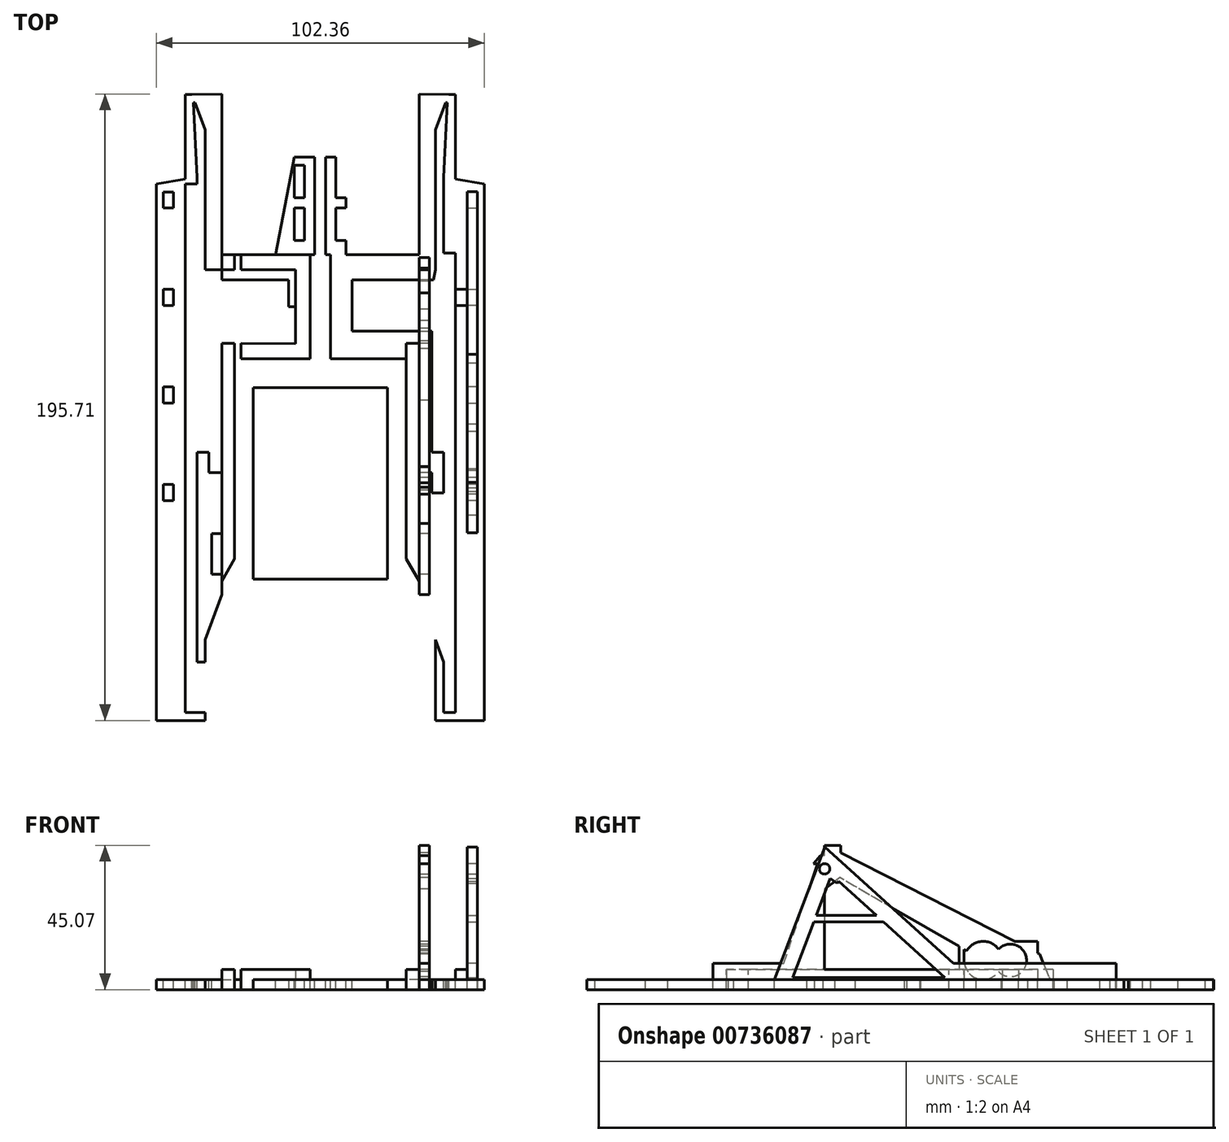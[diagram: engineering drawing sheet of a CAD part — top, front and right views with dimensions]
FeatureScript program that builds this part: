
annotation { "Feature Type Name" : "Feature", "Feature Type Description" : "" }
export const myFeature = defineFeature(function(context is Context, id is Id, definition is map)
    precondition{}
    {
        {
            var Q0;
            Q0=qCreatedBy(makeId("Top.planeOp"),FACE);
            var sketch = newSketch(context, id + "F0", { "sketchPlane" : qUnion([Q0])});
            skLineSegment(sketch, "E0", {"start": v(0, 0) * mm, "end": v(0, -23) * mm});
            skLineSegment(sketch, "E1", {"start": v(0, -23) * mm, "end": v(-4, -23) * mm});
            skLineSegment(sketch, "E2", {"start": v(-4, -23) * mm, "end": v(-4, -27.75) * mm});
            skLineSegment(sketch, "E3", {"start": v(-4, -27.75) * mm, "end": v(-6, -27.75) * mm});
            skLineSegment(sketch, "E4", {"start": v(-6, -27.75) * mm, "end": v(-6, -23) * mm});
            skLineSegment(sketch, "E5", {"start": v(0, -11.5) * mm, "end": v(-23.04, -11.5) * mm});
            skLineSegment(sketch, "E6", {"start": v(-23.04, -11.5) * mm, "end": v(-23.04, -23.02) * mm});
            skLineSegment(sketch, "E7", {"start": v(-23.04, -23.02) * mm, "end": v(-6, -23) * mm});
            skLineSegment(sketch, "E8.MirrorCS", {"start": v(0, 0) * mm, "end": v(-4, 0) * mm});
            skLineSegment(sketch, "E9.MirrorCS", {"start": v(-4, 0) * mm, "end": v(-4, 4.75) * mm});
            skLineSegment(sketch, "E10.MirrorCS", {"start": v(-6, 4.75) * mm, "end": v(-6, 0) * mm});
            skLineSegment(sketch, "E11.MirrorCS", {"start": v(-4, 4.75) * mm, "end": v(-6, 4.75) * mm});
            skLineSegment(sketch, "E12.MirrorCS", {"start": v(-23.04, -11.5) * mm, "end": v(-23.04, 0.02) * mm});
            skLineSegment(sketch, "E13.MirrorCS", {"start": v(-23.04, 0.02) * mm, "end": v(-6, 0) * mm});
            skLineSegment(sketch, "E14", {"start": v(0, -6.14) * mm, "end": v(4, -6.14) * mm});
            skLineSegment(sketch, "E15", {"start": v(0, 0) * mm, "end": v(5.14, 0) * mm});
            skLineSegment(sketch, "E16", {"start": v(5.14, 0) * mm, "end": v(4, -6.14) * mm});
            skLineSegment(sketch, "E17", {"start": v(4, -6.14) * mm, "end": v(7.68, -6.14) * mm});
            skLineSegment(sketch, "E18", {"start": v(7.68, -6.14) * mm, "end": v(7.68, -53.77) * mm});
            skLineSegment(sketch, "E19", {"start": v(7.68, -53.77) * mm, "end": v(7.68, -63.3) * mm});
            skLineSegment(sketch, "E20", {"start": v(7.68, -63.3) * mm, "end": v(0, -63.3) * mm});
            skLineSegment(sketch, "E21", {"start": v(0, -63.3) * mm, "end": v(0, -23) * mm});
            skLineSegment(sketch, "E22", {"start": v(-4, -27.75) * mm, "end": v(-4, -63.3) * mm});
            skLineSegment(sketch, "E23", {"start": v(-4, -63.3) * mm, "end": v(0, -63.3) * mm});
            skLineSegment(sketch, "E24", {"start": v(0, -23) * mm, "end": v(3.18, -23) * mm});
            skLineSegment(sketch, "E25", {"start": v(3.18, -23) * mm, "end": v(3.18, -40.78) * mm});
            skLineSegment(sketch, "E26", {"start": v(3.18, -40.78) * mm, "end": v(0, -40.78) * mm});
            skLineSegment(sketch, "E27", {"start": v(0, -63.3) * mm, "end": v(0, -101.4) * mm});
            skLineSegment(sketch, "E28", {"start": v(0, -101.4) * mm, "end": v(7.68, -122.5) * mm});
            skLineSegment(sketch, "E29", {"start": v(7.68, -122.5) * mm, "end": v(7.68, -63.3) * mm});
            skLineSegment(sketch, "E30", {"start": v(-4, -63.3) * mm, "end": v(-4, -90.28) * mm});
            skLineSegment(sketch, "E31", {"start": v(-4, -90.28) * mm, "end": v(0, -97.2) * mm});
            skLineSegment(sketch, "E32", {"start": v(0, -63.3) * mm, "end": v(3.18, -63.3) * mm});
            skPoint(sketch, "E32.endSnap0", {"position": v(3.18, -31.9) * mm});
            skLineSegment(sketch, "E33", {"start": v(0, -82.34) * mm, "end": v(3.18, -82.34) * mm});
            skLineSegment(sketch, "E34", {"start": v(3.18, -82.34) * mm, "end": v(3.18, -95.04) * mm});
            skLineSegment(sketch, "E35", {"start": v(3.18, -95.04) * mm, "end": v(0, -95.04) * mm});
            skLineSegment(sketch, "E36", {"start": v(7.68, -63.3) * mm, "end": v(11.11, -63.3) * mm});
            skLineSegment(sketch, "E37", {"start": v(7.68, -6.14) * mm, "end": v(7.68, -56.94) * mm});
            skLineSegment(sketch, "E38", {"start": v(7.68, -56.94) * mm, "end": v(4, -56.94) * mm});
            skLineSegment(sketch, "E39", {"start": v(4, -56.94) * mm, "end": v(4, -6.14) * mm});
            skLineSegment(sketch, "E40", {"start": v(4, -56.94) * mm, "end": v(4, -69.64) * mm});
            skLineSegment(sketch, "E41", {"start": v(4, -69.64) * mm, "end": v(7.68, -69.64) * mm});
            skLineSegment(sketch, "E42", {"start": v(0, -23) * mm, "end": v(0, -27.75) * mm});
            skLineSegment(sketch, "E43", {"start": v(-4, -27.75) * mm, "end": v(0, -27.75) * mm});
            skLineSegment(sketch, "E44", {"start": v(-6, -27.75) * mm, "end": v(-27.59, -27.75) * mm});
            skLineSegment(sketch, "E45.MirrorCS", {"start": v(-4, 4.75) * mm, "end": v(0, 4.75) * mm});
            skLineSegment(sketch, "E46.MirrorCS", {"start": v(-6, 4.75) * mm, "end": v(-27.59, 4.75) * mm});
            skLineSegment(sketch, "E47", {"start": v(0, 4.75) * mm, "end": v(0, 0) * mm});
            skLineSegment(sketch, "E48", {"start": v(-27.59, 4.75) * mm, "end": v(-27.59, -27.75) * mm});
            skLineSegment(sketch, "E49", {"start": v(7.68, -56.94) * mm, "end": v(7.68, -138.22) * mm});
            skLineSegment(sketch, "E50", {"start": v(7.68, -138.22) * mm, "end": v(11.37, -138.22) * mm});
            skLineSegment(sketch, "E51", {"start": v(11.37, -138.22) * mm, "end": v(11.37, 24.34) * mm});
            skLineSegment(sketch, "E52", {"start": v(11.37, 24.34) * mm, "end": v(7.68, 24.34) * mm});
            skLineSegment(sketch, "E53", {"start": v(7.68, 24.34) * mm, "end": v(7.68, -6.14) * mm});
            skLineSegment(sketch, "E54", {"start": v(7.68, -122.5) * mm, "end": v(5.14, -122.5) * mm});
            skLineSegment(sketch, "E55", {"start": v(5.14, -122.5) * mm, "end": v(5.14, -115.52) * mm});
            skLineSegment(sketch, "E56", {"start": v(7.68, -138.22) * mm, "end": v(7.68, -140.76) * mm});
            skLineSegment(sketch, "E57", {"start": v(7.68, -138.22) * mm, "end": v(5.14, -138.22) * mm});
            skLineSegment(sketch, "E58", {"start": v(5.14, -122.5) * mm, "end": v(5.14, -140.76) * mm});
            skLineSegment(sketch, "E59", {"start": v(5.14, -140.76) * mm, "end": v(20.38, -140.76) * mm});
            skLineSegment(sketch, "E60", {"start": v(20.38, -140.76) * mm, "end": v(20.38, 24.34) * mm});
            skLineSegment(sketch, "E61", {"start": v(20.38, 24.34) * mm, "end": v(20.38, 26.88) * mm});
            skLineSegment(sketch, "E62", {"start": v(20.38, 26.88) * mm, "end": v(5.14, 26.88) * mm});
            skLineSegment(sketch, "E63", {"start": v(5.14, 26.88) * mm, "end": v(5.14, 0) * mm});
            skLineSegment(sketch, "E64", {"start": v(0, 4.75) * mm, "end": v(0, 30.15) * mm});
            skLineSegment(sketch, "E65", {"start": v(0, 30.15) * mm, "end": v(20.38, 26.88) * mm});
            skLineSegment(sketch, "E66", {"start": v(7.68, 24.34) * mm, "end": v(5.14, 26.88) * mm});
            skLineSegment(sketch, "E67", {"start": v(7.68, 24.34) * mm, "end": v(7.68, 28.92) * mm});
            skLineSegment(sketch, "E68", {"start": v(5.14, 26.88) * mm, "end": v(5.14, 52.28) * mm});
            skLineSegment(sketch, "E69", {"start": v(5.14, 52.28) * mm, "end": v(8.83, 52.28) * mm});
            skLineSegment(sketch, "E70", {"start": v(8.83, 52.28) * mm, "end": v(7.68, 28.92) * mm});
            skLineSegment(sketch, "E71", {"start": v(11.37, 24.34) * mm, "end": v(11.37, 54.82) * mm});
            skLineSegment(sketch, "E72", {"start": v(11.37, 54.82) * mm, "end": v(9.3, 54.82) * mm});
            skLineSegment(sketch, "E73", {"start": v(9.3, 54.82) * mm, "end": v(9.3, 28.66) * mm});
            skLineSegment(sketch, "E74.bottom", {"start": v(-4, -27.75) * mm, "end": v(-57.6, -27.75) * mm});
            skLineSegment(sketch, "E74.top", {"start": v(-4, -96.58) * mm, "end": v(-57.6, -96.58) * mm});
            skLineSegment(sketch, "E74.left", {"start": v(-4, -27.75) * mm, "end": v(-4, -96.58) * mm});
            skLineSegment(sketch, "E74.right", {"start": v(-57.6, -27.75) * mm, "end": v(-57.6, -96.58) * mm});
            skLineSegment(sketch, "E75", {"start": v(-30.8, -96.58) * mm, "end": v(-30.8, -27.75) * mm});
            skLineSegment(sketch, "E76.MirrorCS", {"start": v(-69.28, -6.14) * mm, "end": v(-69.28, -56.94) * mm});
            skLineSegment(sketch, "E77.MirrorCS", {"start": v(-69.28, -6.14) * mm, "end": v(-69.28, -53.77) * mm});
            skLineSegment(sketch, "E78.MirrorCS", {"start": v(-65.6, -56.94) * mm, "end": v(-65.6, -6.14) * mm});
            skLineSegment(sketch, "E79.MirrorCS", {"start": v(-65.6, -6.14) * mm, "end": v(-69.28, -6.14) * mm});
            skLineSegment(sketch, "E80.MirrorCS", {"start": v(-57.6, 4.75) * mm, "end": v(-61.6, 4.75) * mm});
            skLineSegment(sketch, "E81.MirrorCS", {"start": v(-61.6, 0) * mm, "end": v(-66.74, 0) * mm});
            skLineSegment(sketch, "E82.MirrorCS", {"start": v(-61.6, 4.75) * mm, "end": v(-61.6, 0) * mm});
            skLineSegment(sketch, "E83.MirrorCS", {"start": v(-57.6, 4.75) * mm, "end": v(-55.6, 4.75) * mm});
            skLineSegment(sketch, "E84.MirrorCS", {"start": v(-61.6, 0) * mm, "end": v(-57.6, 0) * mm});
            skLineSegment(sketch, "E85.MirrorCS", {"start": v(-57.6, 0) * mm, "end": v(-57.6, 4.75) * mm});
            skLineSegment(sketch, "E86.MirrorCS", {"start": v(-55.6, 4.75) * mm, "end": v(-55.6, 0) * mm});
            skLineSegment(sketch, "E87.MirrorCS", {"start": v(-61.6, -6.14) * mm, "end": v(-65.6, -6.14) * mm});
            skLineSegment(sketch, "E88.MirrorCS", {"start": v(-66.74, 0) * mm, "end": v(-65.6, -6.14) * mm});
            skLineSegment(sketch, "E89.MirrorCS", {"start": v(-61.6, 0) * mm, "end": v(-61.6, -23) * mm});
            skLineSegment(sketch, "E90.MirrorCS", {"start": v(-55.6, 4.75) * mm, "end": v(-34, 4.75) * mm});
            skLineSegment(sketch, "E91.MirrorCS", {"start": v(-61.6, 4.75) * mm, "end": v(-61.6, 30.15) * mm});
            skLineSegment(sketch, "E92.MirrorCS", {"start": v(-34, 4.75) * mm, "end": v(-34, -27.75) * mm});
            skLineSegment(sketch, "E93.MirrorCS", {"start": v(-66.74, 26.88) * mm, "end": v(-66.74, 0) * mm});
            skLineSegment(sketch, "E94.MirrorCS", {"start": v(-72.96, -138.22) * mm, "end": v(-72.96, 24.34) * mm});
            skLineSegment(sketch, "E95.MirrorCS", {"start": v(-81.98, -140.76) * mm, "end": v(-81.98, 24.34) * mm});
            skLineSegment(sketch, "E96.MirrorCS", {"start": v(-69.28, 24.34) * mm, "end": v(-69.28, -6.14) * mm});
            skLineSegment(sketch, "E97.MirrorCS", {"start": v(-38.56, 0.02) * mm, "end": v(-55.6, 0) * mm});
            skLineSegment(sketch, "E98.MirrorCS", {"start": v(-38.56, -11.5) * mm, "end": v(-38.56, 0.02) * mm});
            skLineSegment(sketch, "E99.MirrorCS", {"start": v(-69.28, 24.34) * mm, "end": v(-66.74, 26.88) * mm});
            skLineSegment(sketch, "E100.MirrorCS", {"start": v(-72.96, 24.34) * mm, "end": v(-69.28, 24.34) * mm});
            skLineSegment(sketch, "E101.MirrorCS", {"start": v(-81.98, 24.34) * mm, "end": v(-81.98, 26.88) * mm});
            skLineSegment(sketch, "E102.MirrorCS", {"start": v(-81.98, 26.88) * mm, "end": v(-66.74, 26.88) * mm});
            skLineSegment(sketch, "E103.MirrorCS", {"start": v(-69.28, 24.34) * mm, "end": v(-69.28, 28.92) * mm});
            skLineSegment(sketch, "E104.MirrorCS", {"start": v(-66.74, 52.28) * mm, "end": v(-70.42, 52.28) * mm});
            skLineSegment(sketch, "E105.MirrorCS", {"start": v(-61.6, 30.15) * mm, "end": v(-81.98, 26.88) * mm});
            skLineSegment(sketch, "E106.MirrorCS", {"start": v(-72.96, 24.34) * mm, "end": v(-72.96, 54.82) * mm});
            skLineSegment(sketch, "E107.MirrorCS", {"start": v(-70.42, 52.28) * mm, "end": v(-69.28, 28.92) * mm});
            skLineSegment(sketch, "E108.MirrorCS", {"start": v(-66.74, 26.88) * mm, "end": v(-66.74, 52.28) * mm});
            skLineSegment(sketch, "E109.MirrorCS", {"start": v(-70.9, 54.82) * mm, "end": v(-70.9, 28.66) * mm});
            skLineSegment(sketch, "E110.MirrorCS", {"start": v(-69.28, -138.22) * mm, "end": v(-69.28, -140.76) * mm});
            skLineSegment(sketch, "E111.MirrorCS", {"start": v(-69.28, -138.22) * mm, "end": v(-66.74, -138.22) * mm});
            skLineSegment(sketch, "E112.MirrorCS", {"start": v(-69.28, -122.5) * mm, "end": v(-66.74, -122.5) * mm});
            skLineSegment(sketch, "E113.MirrorCS", {"start": v(-66.74, -140.76) * mm, "end": v(-81.98, -140.76) * mm});
            skLineSegment(sketch, "E114.MirrorCS", {"start": v(-69.28, -138.22) * mm, "end": v(-72.96, -138.22) * mm});
            skLineSegment(sketch, "E115.MirrorCS", {"start": v(-61.6, -101.4) * mm, "end": v(-69.28, -122.5) * mm});
            skLineSegment(sketch, "E116.MirrorCS", {"start": v(-66.74, -122.5) * mm, "end": v(-66.74, -140.76) * mm});
            skLineSegment(sketch, "E117.MirrorCS", {"start": v(-66.74, -122.5) * mm, "end": v(-66.74, -115.52) * mm});
            skLineSegment(sketch, "E118.MirrorCS", {"start": v(-57.6, -63.3) * mm, "end": v(-61.6, -63.3) * mm});
            skLineSegment(sketch, "E119.MirrorCS", {"start": v(-69.28, -56.94) * mm, "end": v(-65.6, -56.94) * mm});
            skLineSegment(sketch, "E120.MirrorCS", {"start": v(-64.77, -23) * mm, "end": v(-64.77, -40.78) * mm});
            skLineSegment(sketch, "E121.MirrorCS", {"start": v(-65.6, -69.64) * mm, "end": v(-69.28, -69.64) * mm});
            skLineSegment(sketch, "E122.MirrorCS", {"start": v(-69.28, -122.5) * mm, "end": v(-69.28, -63.3) * mm});
            skLineSegment(sketch, "E123.MirrorCS", {"start": v(-64.77, -40.78) * mm, "end": v(-61.6, -40.78) * mm});
            skLineSegment(sketch, "E124.MirrorCS", {"start": v(-61.6, -63.3) * mm, "end": v(-64.77, -63.3) * mm});
            skLineSegment(sketch, "E125.MirrorCS", {"start": v(-69.28, -63.3) * mm, "end": v(-72.7, -63.3) * mm});
            skLineSegment(sketch, "E126.MirrorCS", {"start": v(-69.28, -63.3) * mm, "end": v(-61.6, -63.3) * mm});
            skLineSegment(sketch, "E127.MirrorCS", {"start": v(-69.28, -53.77) * mm, "end": v(-69.28, -63.3) * mm});
            skLineSegment(sketch, "E128.MirrorCS", {"start": v(-61.6, -63.3) * mm, "end": v(-61.6, -101.4) * mm});
            skLineSegment(sketch, "E129.MirrorCS", {"start": v(-69.28, -56.94) * mm, "end": v(-69.28, -138.22) * mm});
            skLineSegment(sketch, "E130.MirrorCS", {"start": v(-65.6, -56.94) * mm, "end": v(-65.6, -69.64) * mm});
            skLineSegment(sketch, "E131.MirrorCS", {"start": v(-61.6, -63.3) * mm, "end": v(-61.6, -23) * mm});
            skLineSegment(sketch, "E132.MirrorCS", {"start": v(-57.6, -90.28) * mm, "end": v(-61.6, -97.2) * mm});
            skLineSegment(sketch, "E133.MirrorCS", {"start": v(-61.6, -23) * mm, "end": v(-64.77, -23) * mm});
            skLineSegment(sketch, "E134.MirrorCS", {"start": v(-61.6, -23) * mm, "end": v(-57.6, -23) * mm});
            skLineSegment(sketch, "E135.MirrorCS", {"start": v(-38.56, -23.02) * mm, "end": v(-55.6, -23) * mm});
            skLineSegment(sketch, "E136.MirrorCS", {"start": v(-38.56, -11.5) * mm, "end": v(-38.56, -23.02) * mm});
            skLineSegment(sketch, "E137.MirrorCS", {"start": v(-55.6, -27.75) * mm, "end": v(-55.6, -23) * mm});
            skLineSegment(sketch, "E138.MirrorCS", {"start": v(-57.6, -23) * mm, "end": v(-57.6, -27.75) * mm});
            skLineSegment(sketch, "E139.MirrorCS", {"start": v(-61.6, -11.5) * mm, "end": v(-38.56, -11.5) * mm});
            skLineSegment(sketch, "E140.MirrorCS", {"start": v(-61.6, -23) * mm, "end": v(-61.6, -27.75) * mm});
            skLineSegment(sketch, "E141.MirrorCS", {"start": v(-66.74, 26.88) * mm, "end": v(-66.74, 52.17) * mm});
            skLineSegment(sketch, "E142.MirrorCS", {"start": v(-57.6, -27.75) * mm, "end": v(-61.6, -27.75) * mm});
            skLineSegment(sketch, "E143.MirrorCS", {"start": v(-61.6, -82.34) * mm, "end": v(-64.77, -82.34) * mm});
            skLineSegment(sketch, "E144.MirrorCS", {"start": v(-64.77, -95.04) * mm, "end": v(-61.6, -95.04) * mm});
            skLineSegment(sketch, "E145.MirrorCS", {"start": v(-64.77, -82.34) * mm, "end": v(-64.77, -95.04) * mm});
            skPoint(sketch, "E146.MirrorP", {"position": v(-64.77, -31.9) * mm});
            skLineSegment(sketch, "E147.MirrorCS", {"start": v(-72.96, 54.82) * mm, "end": v(-70.9, 54.82) * mm});
            skLineSegment(sketch, "E148.bottom", {"start": v(-30.8, -96.58) * mm, "end": v(-51.78, -96.58) * mm});
            skLineSegment(sketch, "E148.top", {"start": v(-30.8, -36.78) * mm, "end": v(-51.78, -36.78) * mm});
            skLineSegment(sketch, "E148.left", {"start": v(-30.8, -96.58) * mm, "end": v(-30.8, -36.78) * mm});
            skLineSegment(sketch, "E148.right", {"start": v(-51.78, -96.58) * mm, "end": v(-51.78, -36.78) * mm});
            skLineSegment(sketch, "E149.MirrorCS", {"start": v(-30.8, -36.78) * mm, "end": v(-9.82, -36.78) * mm});
            skLineSegment(sketch, "E150.MirrorCS", {"start": v(-9.82, -96.58) * mm, "end": v(-9.82, -36.78) * mm});
            skLineSegment(sketch, "E151", {"start": v(11.37, 24.34) * mm, "end": v(15.05, 24.34) * mm});
            skLineSegment(sketch, "E152", {"start": v(15.05, 24.34) * mm, "end": v(18.27, 24.34) * mm});
            skLineSegment(sketch, "E153", {"start": v(18.27, 24.34) * mm, "end": v(20.38, 24.34) * mm});
            skLineSegment(sketch, "E154", {"start": v(15.05, 24.34) * mm, "end": v(15.05, 19.36) * mm});
            skLineSegment(sketch, "E155", {"start": v(15.05, 19.36) * mm, "end": v(18.27, 19.36) * mm});
            skLineSegment(sketch, "E156", {"start": v(18.27, 19.36) * mm, "end": v(18.27, 24.34) * mm});
            skLineSegment(sketch, "E157", {"start": v(16.66, 19.36) * mm, "end": v(16.66, -6.04) * mm});
            skLineSegment(sketch, "E158", {"start": v(16.66, -6.04) * mm, "end": v(18.27, -6.04) * mm});
            skLineSegment(sketch, "E159", {"start": v(18.27, -6.04) * mm, "end": v(18.27, -11.12) * mm});
            skLineSegment(sketch, "E160", {"start": v(18.27, -11.12) * mm, "end": v(15.05, -11.12) * mm});
            skLineSegment(sketch, "E161", {"start": v(15.05, -11.12) * mm, "end": v(15.05, -6.04) * mm});
            skLineSegment(sketch, "E162", {"start": v(15.05, -6.04) * mm, "end": v(16.66, -6.04) * mm});
            skLineSegment(sketch, "E163", {"start": v(16.66, -11.12) * mm, "end": v(16.66, -36.52) * mm});
            skLineSegment(sketch, "E164", {"start": v(16.66, -36.52) * mm, "end": v(18.27, -36.52) * mm});
            skLineSegment(sketch, "E165", {"start": v(18.27, -36.52) * mm, "end": v(15.05, -36.52) * mm});
            skLineSegment(sketch, "E166", {"start": v(15.05, -36.52) * mm, "end": v(15.05, -41.6) * mm});
            skLineSegment(sketch, "E167", {"start": v(15.05, -41.6) * mm, "end": v(18.27, -41.6) * mm});
            skLineSegment(sketch, "E168", {"start": v(18.27, -41.6) * mm, "end": v(18.27, -36.52) * mm});
            skLineSegment(sketch, "E169", {"start": v(15.05, -39.06) * mm, "end": v(18.27, -39.06) * mm});
            skLineSegment(sketch, "E170.MirrorCS", {"start": v(16.66, -67) * mm, "end": v(16.66, -41.6) * mm});
            skLineSegment(sketch, "E171.MirrorCS", {"start": v(18.27, -41.6) * mm, "end": v(15.05, -41.6) * mm});
            skLineSegment(sketch, "E172.MirrorCS", {"start": v(15.05, -41.6) * mm, "end": v(15.05, -36.52) * mm});
            skLineSegment(sketch, "E173", {"start": v(16.66, -67) * mm, "end": v(18.27, -67) * mm});
            skLineSegment(sketch, "E174", {"start": v(16.66, -67) * mm, "end": v(16.66, -54.3) * mm});
            skLineSegment(sketch, "E175", {"start": v(16.66, -67) * mm, "end": v(15.07, -67) * mm});
            skLineSegment(sketch, "E176", {"start": v(18.27, -67) * mm, "end": v(18.27, -72.08) * mm});
            skLineSegment(sketch, "E177", {"start": v(18.27, -72.08) * mm, "end": v(15.05, -72.08) * mm});
            skLineSegment(sketch, "E178", {"start": v(15.05, -72.08) * mm, "end": v(15.07, -67) * mm});
            skLineSegment(sketch, "E179", {"start": v(0, 30.15) * mm, "end": v(9.3, 54.82) * mm});
            skLineSegment(sketch, "E180", {"start": v(0, 30.15) * mm, "end": v(0, 54.95) * mm});
            skLineSegment(sketch, "E181", {"start": v(0, 54.95) * mm, "end": v(9.3, 54.82) * mm});
            skLineSegment(sketch, "E182.MirrorCS", {"start": v(-72.96, 24.34) * mm, "end": v(-76.64, 24.34) * mm});
            skLineSegment(sketch, "E183.MirrorCS", {"start": v(-79.87, 19.36) * mm, "end": v(-79.87, 24.34) * mm});
            skLineSegment(sketch, "E184.MirrorCS", {"start": v(-76.64, 24.34) * mm, "end": v(-76.64, 19.36) * mm});
            skLineSegment(sketch, "E185.MirrorCS", {"start": v(-76.64, 24.34) * mm, "end": v(-79.87, 24.34) * mm});
            skLineSegment(sketch, "E186.MirrorCS", {"start": v(-76.64, 19.36) * mm, "end": v(-79.87, 19.36) * mm});
            skLineSegment(sketch, "E187.MirrorCS", {"start": v(-79.87, 24.34) * mm, "end": v(-81.98, 24.34) * mm});
            skLineSegment(sketch, "E188.MirrorCS", {"start": v(-76.64, -36.52) * mm, "end": v(-76.64, -41.6) * mm});
            skLineSegment(sketch, "E189.MirrorCS", {"start": v(-57.6, -27.75) * mm, "end": v(-55.6, -27.75) * mm});
            skLineSegment(sketch, "E190.MirrorCS", {"start": v(-61.6, 54.95) * mm, "end": v(-70.9, 54.82) * mm});
            skLineSegment(sketch, "E191.MirrorCS", {"start": v(-76.64, -41.6) * mm, "end": v(-79.87, -41.6) * mm});
            skLineSegment(sketch, "E192.MirrorCS", {"start": v(-78.26, -36.52) * mm, "end": v(-79.87, -36.52) * mm});
            skLineSegment(sketch, "E193.MirrorCS", {"start": v(-79.87, -36.52) * mm, "end": v(-76.64, -36.52) * mm});
            skLineSegment(sketch, "E194.MirrorCS", {"start": v(-79.87, -41.6) * mm, "end": v(-79.87, -36.52) * mm});
            skLineSegment(sketch, "E195.MirrorCS", {"start": v(-76.64, -11.12) * mm, "end": v(-76.64, -6.04) * mm});
            skLineSegment(sketch, "E196.MirrorCS", {"start": v(-76.64, -41.6) * mm, "end": v(-76.64, -36.52) * mm});
            skLineSegment(sketch, "E197.MirrorCS", {"start": v(-76.64, -39.06) * mm, "end": v(-79.87, -39.06) * mm});
            skLineSegment(sketch, "E198.MirrorCS", {"start": v(-79.87, -41.6) * mm, "end": v(-76.64, -41.6) * mm});
            skLineSegment(sketch, "E199.MirrorCS", {"start": v(-76.64, -72.08) * mm, "end": v(-76.67, -67) * mm});
            skLineSegment(sketch, "E200.MirrorCS", {"start": v(-78.26, -67) * mm, "end": v(-79.87, -67) * mm});
            skLineSegment(sketch, "E201.MirrorCS", {"start": v(-78.26, -67) * mm, "end": v(-76.67, -67) * mm});
            skLineSegment(sketch, "E202.MirrorCS", {"start": v(-78.26, -67) * mm, "end": v(-78.26, -54.3) * mm});
            skLineSegment(sketch, "E203.MirrorCS", {"start": v(-78.26, -67) * mm, "end": v(-78.26, -41.6) * mm});
            skLineSegment(sketch, "E204.MirrorCS", {"start": v(-79.87, -11.12) * mm, "end": v(-76.64, -11.12) * mm});
            skLineSegment(sketch, "E205.MirrorCS", {"start": v(-79.87, -72.08) * mm, "end": v(-76.64, -72.08) * mm});
            skLineSegment(sketch, "E206.MirrorCS", {"start": v(-76.64, -6.04) * mm, "end": v(-78.26, -6.04) * mm});
            skLineSegment(sketch, "E207.MirrorCS", {"start": v(-79.87, -67) * mm, "end": v(-79.87, -72.08) * mm});
            skLineSegment(sketch, "E208.MirrorCS", {"start": v(-78.26, -6.04) * mm, "end": v(-79.87, -6.04) * mm});
            skLineSegment(sketch, "E209.MirrorCS", {"start": v(-79.87, -6.04) * mm, "end": v(-79.87, -11.12) * mm});
            skLineSegment(sketch, "E210.MirrorCS", {"start": v(-57.6, -27.75) * mm, "end": v(-4, -27.75) * mm});
            skLineSegment(sketch, "E211.MirrorCS", {"start": v(-55.6, -27.75) * mm, "end": v(-34, -27.75) * mm});
            skLineSegment(sketch, "E212.MirrorCS", {"start": v(-57.6, -63.3) * mm, "end": v(-57.6, -90.28) * mm});
            skLineSegment(sketch, "E213.MirrorCS", {"start": v(-57.6, -27.75) * mm, "end": v(-57.6, -63.3) * mm});
            skLineSegment(sketch, "E214.MirrorCS", {"start": v(-61.6, 30.15) * mm, "end": v(-61.6, 54.95) * mm});
            skLineSegment(sketch, "E215.MirrorCS", {"start": v(-78.26, -11.12) * mm, "end": v(-78.26, -36.52) * mm});
            skLineSegment(sketch, "E216.MirrorCS", {"start": v(-61.6, 30.15) * mm, "end": v(-70.9, 54.82) * mm});
            skLineSegment(sketch, "E217.MirrorCS", {"start": v(-78.26, 19.36) * mm, "end": v(-78.26, -6.04) * mm});
            skLineSegment(sketch, "E218.MirrorCS", {"start": v(-57.6, -96.58) * mm, "end": v(-4, -96.58) * mm});
            skLineSegment(sketch, "E219", {"start": v(7.68, 5.2) * mm, "end": v(11.37, 5.2) * mm});
            skLineSegment(sketch, "E220.MirrorCS", {"start": v(-69.28, 5.2) * mm, "end": v(-72.96, 5.2) * mm});
            skLineSegment(sketch, "E221", {"start": v(15.05, -6.04) * mm, "end": v(11.37, -6.04) * mm});
            skLineSegment(sketch, "E222", {"start": v(15.05, -11.12) * mm, "end": v(11.37, -11.12) * mm});
            skLineSegment(sketch, "E223", {"start": v(-34, 4.75) * mm, "end": v(-27.59, 4.75) * mm});
            skLineSegment(sketch, "E224", {"start": v(-30.8, 4.75) * mm, "end": v(-30.8, 80.95) * mm});
            skPoint(sketch, "E224.endSnap0", {"position": v(-30.8, 4.75) * mm});
            skLineSegment(sketch, "E225", {"start": v(-16.8, 4.75) * mm, "end": v(-16.8, 35.23) * mm});
            skLineSegment(sketch, "E226", {"start": v(-16.8, 35.23) * mm, "end": v(-30.8, 35.23) * mm});
            skLineSegment(sketch, "E227.MirrorCS", {"start": v(-44.8, 35.23) * mm, "end": v(-30.8, 35.23) * mm});
            skLineSegment(sketch, "E228.MirrorCS", {"start": v(-44.8, 4.75) * mm, "end": v(-44.8, 35.23) * mm});
            skLineSegment(sketch, "E229", {"start": v(-30.8, 35.23) * mm, "end": v(-29.08, 35.23) * mm});
            skLineSegment(sketch, "E230", {"start": v(-29.08, 35.23) * mm, "end": v(-29.08, 4.75) * mm});
            skLineSegment(sketch, "E231.MirrorCS", {"start": v(-32.51, 35.23) * mm, "end": v(-32.51, 4.75) * mm});
            skLineSegment(sketch, "E232", {"start": v(-29.08, 4.75) * mm, "end": v(-25.9, 4.75) * mm});
            skLineSegment(sketch, "E233", {"start": v(-25.9, 4.75) * mm, "end": v(-22.73, 4.75) * mm});
            skLineSegment(sketch, "E234", {"start": v(-22.73, 4.75) * mm, "end": v(-22.73, 35.23) * mm});
            skLineSegment(sketch, "E235.MirrorCS", {"start": v(-38.86, 4.75) * mm, "end": v(-38.86, 35.23) * mm});
            skLineSegment(sketch, "E236", {"start": v(-22.73, 35.23) * mm, "end": v(-25.9, 35.23) * mm});
            skLineSegment(sketch, "E237", {"start": v(-25.9, 35.23) * mm, "end": v(-25.9, 32.7) * mm});
            skLineSegment(sketch, "E238", {"start": v(-25.9, 32.7) * mm, "end": v(-22.73, 32.7) * mm});
            skLineSegment(sketch, "E239", {"start": v(-22.73, 32.7) * mm, "end": v(-22.73, 22.53) * mm});
            skLineSegment(sketch, "E240", {"start": v(-22.73, 22.53) * mm, "end": v(-25.9, 22.53) * mm});
            skLineSegment(sketch, "E241", {"start": v(-25.9, 22.53) * mm, "end": v(-25.9, 32.7) * mm});
            skLineSegment(sketch, "E242", {"start": v(-25.9, 22.53) * mm, "end": v(-25.9, 19.36) * mm});
            skLineSegment(sketch, "E243", {"start": v(-25.9, 19.36) * mm, "end": v(-22.73, 19.36) * mm});
            skLineSegment(sketch, "E244", {"start": v(-22.73, 19.36) * mm, "end": v(-22.73, 9.2) * mm});
            skLineSegment(sketch, "E245", {"start": v(-22.73, 9.2) * mm, "end": v(-25.9, 9.2) * mm});
            skLineSegment(sketch, "E246", {"start": v(-25.9, 9.2) * mm, "end": v(-25.9, 19.36) * mm});
            skLineSegment(sketch, "E247.MirrorCS", {"start": v(-35.69, 32.7) * mm, "end": v(-38.86, 32.7) * mm});
            skLineSegment(sketch, "E248.MirrorCS", {"start": v(-38.86, 22.53) * mm, "end": v(-35.69, 22.53) * mm});
            skLineSegment(sketch, "E249.MirrorCS", {"start": v(-35.69, 22.53) * mm, "end": v(-35.69, 32.7) * mm});
            skLineSegment(sketch, "E250.MirrorCS", {"start": v(-38.86, 9.2) * mm, "end": v(-35.69, 9.2) * mm});
            skLineSegment(sketch, "E251.MirrorCS", {"start": v(-35.69, 9.2) * mm, "end": v(-35.69, 19.36) * mm});
            skLineSegment(sketch, "E252.MirrorCS", {"start": v(-35.69, 19.36) * mm, "end": v(-38.86, 19.36) * mm});
            skLineSegment(sketch, "E253", {"start": v(-44.8, 4.75) * mm, "end": v(-38.86, 35.23) * mm});
            skLineSegment(sketch, "E254", {"start": v(-22.73, 35.23) * mm, "end": v(-16.8, 4.75) * mm});
            skSolve(sketch);
        }
        {
            var Q0;
            {var subQ2=sQuery(id+"F0.wireOp",EDGE,"E75");Q0=makeQuery(id+"F0.imprint","IMPRINT",FACE,{"disambiguationData":[TD([[makeQuery(id+"F0.imprint","IMPRINT",EDGE,{"derivedFrom":subQ2}),1.0]])]});}
            var Q1;
            {var subQ21=sQuery(id+"F0.wireOp",EDGE,"E110.MirrorCS");Q1=makeQuery(id+"F0.imprint","IMPRINT",FACE,{"disambiguationData":[TD([[makeQuery(id+"F0.imprint","IMPRINT",EDGE,{"derivedFrom":subQ21}),-1.0]])]});}
            var Q2;
            {var subQ1=sQuery(id+"F0.wireOp",EDGE,"E151");Q2=makeQuery(id+"F0.imprint","IMPRINT",FACE,{"disambiguationData":[TD([[makeQuery(id+"F0.imprint","IMPRINT",EDGE,{"derivedFrom":subQ1}),-1.0]])]});}
            var Q3;
            Q3=makeQuery(id+"F0.imprint","IMPRINT",FACE,{"disambiguationData":[TD([[makeQuery(id+"F0.imprint","IMPRINT",EDGE,{"derivedFrom":sQuery(id+"F0.wireOp",EDGE,"E92.MirrorCS")}),-1.0]])]});
            var Q4;
            {var subQ6=sQuery(id+"F0.wireOp",EDGE,"E121.MirrorCS");Q4=makeQuery(id+"F0.imprint","IMPRINT",FACE,{"disambiguationData":[TD([[makeQuery(id+"F0.imprint","IMPRINT",EDGE,{"derivedFrom":subQ6}),1.0]])]});}
            var Q5;
            {var subQ0=sQuery(id+"F0.wireOp",EDGE,"E75");Q5=makeQuery(id+"F0.imprint","IMPRINT",FACE,{"disambiguationData":[TD([[makeQuery(id+"F0.imprint","IMPRINT",EDGE,{"derivedFrom":subQ0}),-1.0]])]});}
            var Q6;
            {var subQ0=sQuery(id+"F0.wireOp",EDGE,"E52");Q6=makeQuery(id+"F0.imprint","IMPRINT",FACE,{"disambiguationData":[TD([[makeQuery(id+"F0.imprint","IMPRINT",EDGE,{"derivedFrom":subQ0}),1.0]])]});}
            var Q7;
            {var subQ2=sQuery(id+"F0.wireOp",EDGE,"E32");Q7=makeQuery(id+"F0.imprint","IMPRINT",FACE,{"disambiguationData":[TD([[makeQuery(id+"F0.imprint","IMPRINT",EDGE,{"derivedFrom":subQ2}),-1.0]])]});}
            var Q8;
            {var subQ0=sQuery(id+"F0.wireOp",EDGE,"E100.MirrorCS");Q8=makeQuery(id+"F0.imprint","IMPRINT",FACE,{"disambiguationData":[TD([[makeQuery(id+"F0.imprint","IMPRINT",EDGE,{"derivedFrom":subQ0}),-1.0]])]});}
            var Q9;
            {var subQ1=sQuery(id+"F0.wireOp",EDGE,"E4");Q9=makeQuery(id+"F0.imprint","IMPRINT",FACE,{"disambiguationData":[TD([[makeQuery(id+"F0.imprint","IMPRINT",EDGE,{"derivedFrom":subQ1}),1.0]])]});}
            var Q10;
            {var subQ3=sQuery(id+"F0.wireOp",EDGE,"E104.MirrorCS");Q10=makeQuery(id+"F0.imprint","IMPRINT",FACE,{"disambiguationData":[TD([[makeQuery(id+"F0.imprint","IMPRINT",EDGE,{"derivedFrom":subQ3}),-1.0]])]});}
            var Q11;
            {var subQ4=sQuery(id+"F0.wireOp",EDGE,"E72");Q11=makeQuery(id+"F0.imprint","IMPRINT",FACE,{"disambiguationData":[TD([[makeQuery(id+"F0.imprint","IMPRINT",EDGE,{"derivedFrom":subQ4}),1.0]])]});}
            var Q12;
            {var subQ3=sQuery(id+"F0.wireOp",EDGE,"E73");Q12=makeQuery(id+"F0.imprint","IMPRINT",FACE,{"disambiguationData":[TD([[makeQuery(id+"F0.imprint","IMPRINT",EDGE,{"derivedFrom":subQ3}),-1.0]])]});}
            var Q13;
            {var subQ1=sQuery(id+"F0.wireOp",EDGE,"E23");Q13=makeQuery(id+"F0.imprint","IMPRINT",FACE,{"disambiguationData":[TD([[makeQuery(id+"F0.imprint","IMPRINT",EDGE,{"derivedFrom":subQ1}),1.0]])]});}
            var Q14;
            {var subQ7=sQuery(id+"F0.wireOp",EDGE,"E14");Q14=makeQuery(id+"F0.imprint","IMPRINT",FACE,{"disambiguationData":[TD([[makeQuery(id+"F0.imprint","IMPRINT",EDGE,{"derivedFrom":subQ7}),-1.0]])]});}
            var Q15;
            Q15=makeQuery(id+"F0.imprint","IMPRINT",FACE,{"disambiguationData":[TD([[makeQuery(id+"F0.imprint","IMPRINT",EDGE,{"derivedFrom":sQuery(id+"F0.wireOp",EDGE,"E15")}),1.0]])]});
            var Q16;
            {var subQ5=sQuery(id+"F0.wireOp",EDGE,"E69");Q16=makeQuery(id+"F0.imprint","IMPRINT",FACE,{"disambiguationData":[TD([[makeQuery(id+"F0.imprint","IMPRINT",EDGE,{"derivedFrom":subQ5}),1.0]])]});}
            var Q17;
            {var subQ1=sQuery(id+"F0.wireOp",EDGE,"E65");var subQ3=sQuery(id+"F0.wireOp",EDGE,"E68");var subQ4=makeQuery(id+"F0.imprint","INTERSECT",VERTEX,{"derivedFrom":[subQ1,subQ3]});Q17=makeQuery(id+"F0.imprint","IMPRINT",FACE,{"disambiguationData":[TD([[makeQuery(id+"F0.imprint","IMPRINT",EDGE,{"disambiguationData":[TD([[subQ4,-1.0]])],"derivedFrom":subQ3}),1.0]])]});}
            var Q18;
            {var subQ1=sQuery(id+"F0.wireOp",EDGE,"E105.MirrorCS");var subQ3=sQuery(id+"F0.wireOp",EDGE,"E108.MirrorCS");var subQ4=makeQuery(id+"F0.imprint","INTERSECT",VERTEX,{"derivedFrom":[subQ1,subQ3]});Q18=makeQuery(id+"F0.imprint","IMPRINT",FACE,{"disambiguationData":[TD([[makeQuery(id+"F0.imprint","IMPRINT",EDGE,{"disambiguationData":[TD([[subQ4,-1.0]])],"derivedFrom":subQ3}),-1.0]])]});}
            var Q19;
            {var subQ3=sQuery(id+"F0.wireOp",EDGE,"E23");Q19=makeQuery(id+"F0.imprint","IMPRINT",FACE,{"disambiguationData":[TD([[makeQuery(id+"F0.imprint","IMPRINT",EDGE,{"derivedFrom":subQ3}),-1.0]])]});}
            var Q20;
            {var subQ0=sQuery(id+"F0.wireOp",EDGE,"E54");Q20=makeQuery(id+"F0.imprint","IMPRINT",FACE,{"disambiguationData":[TD([[makeQuery(id+"F0.imprint","IMPRINT",EDGE,{"derivedFrom":subQ0}),-1.0]])]});}
            var Q21;
            {var subQ3=sQuery(id+"F0.wireOp",EDGE,"E109.MirrorCS");Q21=makeQuery(id+"F0.imprint","IMPRINT",FACE,{"disambiguationData":[TD([[makeQuery(id+"F0.imprint","IMPRINT",EDGE,{"derivedFrom":subQ3}),1.0]])]});}
            var Q22;
            {var subQ5=sQuery(id+"F0.wireOp",EDGE,"E41");Q22=makeQuery(id+"F0.imprint","IMPRINT",FACE,{"disambiguationData":[TD([[makeQuery(id+"F0.imprint","IMPRINT",EDGE,{"derivedFrom":subQ5}),1.0]])]});}
            var Q23;
            {var subQ4=sQuery(id+"F0.wireOp",EDGE,"E118.MirrorCS");Q23=makeQuery(id+"F0.imprint","IMPRINT",FACE,{"disambiguationData":[TD([[makeQuery(id+"F0.imprint","IMPRINT",EDGE,{"derivedFrom":subQ4}),1.0]])]});}
            var Q24;
            {var subQ0=sQuery(id+"F0.wireOp",EDGE,"E147.MirrorCS");Q24=makeQuery(id+"F0.imprint","IMPRINT",FACE,{"disambiguationData":[TD([[makeQuery(id+"F0.imprint","IMPRINT",EDGE,{"derivedFrom":subQ0}),-1.0]])]});}
            var Q25;
            {var subQ2=sQuery(id+"F0.wireOp",EDGE,"E71");var subQ6=sQuery(id+"F0.wireOp",EDGE,"E62");var subQ8=makeQuery(id+"F0.imprint","INTERSECT",VERTEX,{"derivedFrom":[subQ6,subQ2]});Q25=makeQuery(id+"F0.imprint","IMPRINT",FACE,{"disambiguationData":[TD([[makeQuery(id+"F0.imprint","IMPRINT",EDGE,{"disambiguationData":[TD([[subQ8,-1.0]])],"derivedFrom":subQ6}),-1.0]])]});}
            var Q26;
            {var subQ5=sQuery(id+"F0.wireOp",EDGE,"E38");Q26=makeQuery(id+"F0.imprint","IMPRINT",FACE,{"disambiguationData":[TD([[makeQuery(id+"F0.imprint","IMPRINT",EDGE,{"derivedFrom":subQ5}),1.0]])]});}
            var Q27;
            Q27=makeQuery(id+"F0.imprint","IMPRINT",FACE,{"disambiguationData":[TD([[makeQuery(id+"F0.imprint","IMPRINT",EDGE,{"derivedFrom":sQuery(id+"F0.wireOp",EDGE,"E161")}),1.0]])]});
            var Q28;
            {var subQ0=sQuery(id+"F0.wireOp",EDGE,"E65");var subQ3=sQuery(id+"F0.wireOp",EDGE,"E71");var subQ5=makeQuery(id+"F0.imprint","INTERSECT",VERTEX,{"derivedFrom":[subQ0,subQ3]});Q28=makeQuery(id+"F0.imprint","IMPRINT",FACE,{"disambiguationData":[TD([[makeQuery(id+"F0.imprint","IMPRINT",EDGE,{"disambiguationData":[TD([[subQ5,1.0]])],"derivedFrom":subQ3}),-1.0]])]});}
            var Q29;
            Q29=makeQuery(id+"F0.imprint","IMPRINT",FACE,{"disambiguationData":[TD([[makeQuery(id+"F0.imprint","IMPRINT",EDGE,{"derivedFrom":sQuery(id+"F0.wireOp",EDGE,"E8.MirrorCS")}),-1.0]])]});
            var Q30;
            {var subQ0=sQuery(id+"F0.wireOp",EDGE,"E52");Q30=makeQuery(id+"F0.imprint","IMPRINT",FACE,{"disambiguationData":[TD([[makeQuery(id+"F0.imprint","IMPRINT",EDGE,{"derivedFrom":subQ0}),-1.0]])]});}
            var Q31;
            {var subQ2=sQuery(id+"F0.wireOp",EDGE,"E14");Q31=makeQuery(id+"F0.imprint","IMPRINT",FACE,{"disambiguationData":[TD([[makeQuery(id+"F0.imprint","IMPRINT",EDGE,{"derivedFrom":subQ2}),1.0]])]});}
            var Q32;
            {var subQ2=sQuery(id+"F0.wireOp",EDGE,"E61");Q32=makeQuery(id+"F0.imprint","IMPRINT",FACE,{"disambiguationData":[TD([[makeQuery(id+"F0.imprint","IMPRINT",EDGE,{"derivedFrom":subQ2}),1.0]])]});}
            var Q33;
            {var subQ0=sQuery(id+"F0.wireOp",EDGE,"E112.MirrorCS");Q33=makeQuery(id+"F0.imprint","IMPRINT",FACE,{"disambiguationData":[TD([[makeQuery(id+"F0.imprint","IMPRINT",EDGE,{"derivedFrom":subQ0}),1.0]])]});}
            var Q34;
            Q34=makeQuery(id+"F0.imprint","IMPRINT",FACE,{"disambiguationData":[TD([[makeQuery(id+"F0.imprint","IMPRINT",EDGE,{"derivedFrom":sQuery(id+"F0.wireOp",EDGE,"E1")}),1.0]])]});
            var Q35;
            {var subQ0=sQuery(id+"F0.wireOp",EDGE,"E121.MirrorCS");Q35=makeQuery(id+"F0.imprint","IMPRINT",FACE,{"disambiguationData":[TD([[makeQuery(id+"F0.imprint","IMPRINT",EDGE,{"derivedFrom":subQ0}),-1.0]])]});}
            var Q36;
            {var subQ0=sQuery(id+"F0.wireOp",EDGE,"E105.MirrorCS");var subQ3=sQuery(id+"F0.wireOp",EDGE,"E106.MirrorCS");var subQ5=makeQuery(id+"F0.imprint","INTERSECT",VERTEX,{"derivedFrom":[subQ0,subQ3]});Q36=makeQuery(id+"F0.imprint","IMPRINT",FACE,{"disambiguationData":[TD([[makeQuery(id+"F0.imprint","IMPRINT",EDGE,{"disambiguationData":[TD([[subQ5,1.0]])],"derivedFrom":subQ3}),1.0]])]});}
            var Q37;
            {var subQ2=sQuery(id+"F0.wireOp",EDGE,"E106.MirrorCS");var subQ6=sQuery(id+"F0.wireOp",EDGE,"E102.MirrorCS");var subQ8=makeQuery(id+"F0.imprint","INTERSECT",VERTEX,{"derivedFrom":[subQ6,subQ2]});Q37=makeQuery(id+"F0.imprint","IMPRINT",FACE,{"disambiguationData":[TD([[makeQuery(id+"F0.imprint","IMPRINT",EDGE,{"disambiguationData":[TD([[subQ8,-1.0]])],"derivedFrom":subQ6}),1.0]])]});}
            var Q38;
            Q38=makeQuery(id+"F0.imprint","IMPRINT",FACE,{"disambiguationData":[TD([[makeQuery(id+"F0.imprint","IMPRINT",EDGE,{"derivedFrom":sQuery(id+"F0.wireOp",EDGE,"E88.MirrorCS")}),1.0]])]});
            var Q39;
            {var subQ4=sQuery(id+"F0.wireOp",EDGE,"E182.MirrorCS");Q39=makeQuery(id+"F0.imprint","IMPRINT",FACE,{"disambiguationData":[TD([[makeQuery(id+"F0.imprint","IMPRINT",EDGE,{"derivedFrom":subQ4}),-1.0]])]});}
            var Q40;
            {var subQ5=sQuery(id+"F0.wireOp",EDGE,"E100.MirrorCS");Q40=makeQuery(id+"F0.imprint","IMPRINT",FACE,{"disambiguationData":[TD([[makeQuery(id+"F0.imprint","IMPRINT",EDGE,{"derivedFrom":subQ5}),1.0]])]});}
            var Q41;
            {var subQ0=sQuery(id+"F0.wireOp",EDGE,"E142.MirrorCS");Q41=makeQuery(id+"F0.imprint","IMPRINT",FACE,{"disambiguationData":[TD([[makeQuery(id+"F0.imprint","IMPRINT",EDGE,{"derivedFrom":subQ0}),-1.0]])]});}
            var Q42;
            {var subQ5=sQuery(id+"F0.wireOp",EDGE,"E119.MirrorCS");Q42=makeQuery(id+"F0.imprint","IMPRINT",FACE,{"disambiguationData":[TD([[makeQuery(id+"F0.imprint","IMPRINT",EDGE,{"derivedFrom":subQ5}),-1.0]])]});}
            var Q43;
            Q43=makeQuery(id+"F0.imprint","IMPRINT",FACE,{"disambiguationData":[TD([[makeQuery(id+"F0.imprint","IMPRINT",EDGE,{"derivedFrom":sQuery(id+"F0.wireOp",EDGE,"E84.MirrorCS")}),1.0]])]});
            var Q44;
            {var subQ2=sQuery(id+"F0.wireOp",EDGE,"E1");Q44=makeQuery(id+"F0.imprint","IMPRINT",FACE,{"disambiguationData":[TD([[makeQuery(id+"F0.imprint","IMPRINT",EDGE,{"derivedFrom":subQ2}),-1.0]])]});}
            var Q45;
            {var subQ1=sQuery(id+"F0.wireOp",EDGE,"E5");Q45=makeQuery(id+"F0.imprint","IMPRINT",FACE,{"disambiguationData":[TD([[makeQuery(id+"F0.imprint","IMPRINT",EDGE,{"derivedFrom":subQ1}),-1.0]])]});}
            var Q46;
            {var subQ3=sQuery(id+"F0.wireOp",EDGE,"E84.MirrorCS");Q46=makeQuery(id+"F0.imprint","IMPRINT",FACE,{"disambiguationData":[TD([[makeQuery(id+"F0.imprint","IMPRINT",EDGE,{"derivedFrom":subQ3}),-1.0]])]});}
            var Q47;
            {var subQ1=sQuery(id+"F0.wireOp",EDGE,"E134.MirrorCS");Q47=makeQuery(id+"F0.imprint","IMPRINT",FACE,{"disambiguationData":[TD([[makeQuery(id+"F0.imprint","IMPRINT",EDGE,{"derivedFrom":subQ1}),1.0]])]});}
            var Q48;
            {var subQ1=sQuery(id+"F0.wireOp",EDGE,"E142.MirrorCS");Q48=makeQuery(id+"F0.imprint","IMPRINT",FACE,{"disambiguationData":[TD([[makeQuery(id+"F0.imprint","IMPRINT",EDGE,{"derivedFrom":subQ1}),1.0]])]});}
            var Q49;
            {var subQ19=sQuery(id+"F0.wireOp",EDGE,"E50");Q49=makeQuery(id+"F0.imprint","IMPRINT",FACE,{"disambiguationData":[TD([[makeQuery(id+"F0.imprint","IMPRINT",EDGE,{"derivedFrom":subQ19}),-1.0]])]});}
            var Q50;
            {var subQ0=sQuery(id+"F0.wireOp",EDGE,"E69");Q50=makeQuery(id+"F0.imprint","IMPRINT",FACE,{"disambiguationData":[TD([[makeQuery(id+"F0.imprint","IMPRINT",EDGE,{"derivedFrom":subQ0}),-1.0]])]});}
            var Q51;
            {var subQ0=sQuery(id+"F0.wireOp",EDGE,"E104.MirrorCS");Q51=makeQuery(id+"F0.imprint","IMPRINT",FACE,{"disambiguationData":[TD([[makeQuery(id+"F0.imprint","IMPRINT",EDGE,{"derivedFrom":subQ0}),1.0]])]});}
            var Q52;
            {var subQ2=sQuery(id+"F0.wireOp",EDGE,"E133.MirrorCS");Q52=makeQuery(id+"F0.imprint","IMPRINT",FACE,{"disambiguationData":[TD([[makeQuery(id+"F0.imprint","IMPRINT",EDGE,{"derivedFrom":subQ2}),-1.0]])]});}
            var Q53;
            Q53=makeQuery(id+"F0.imprint","IMPRINT",FACE,{"disambiguationData":[TD([[makeQuery(id+"F0.imprint","IMPRINT",EDGE,{"derivedFrom":sQuery(id+"F0.wireOp",EDGE,"E81.MirrorCS")}),-1.0]])]});
            var Q54;
            {var subQ0=sQuery(id+"F0.wireOp",EDGE,"E111.MirrorCS");Q54=makeQuery(id+"F0.imprint","IMPRINT",FACE,{"disambiguationData":[TD([[makeQuery(id+"F0.imprint","IMPRINT",EDGE,{"derivedFrom":subQ0}),1.0]])]});}
            var Q55;
            {var subQ0=sQuery(id+"F0.wireOp",EDGE,"E110.MirrorCS");Q55=makeQuery(id+"F0.imprint","IMPRINT",FACE,{"disambiguationData":[TD([[makeQuery(id+"F0.imprint","IMPRINT",EDGE,{"derivedFrom":subQ0}),1.0]])]});}
            var Q56;
            {var subQ0=sQuery(id+"F0.wireOp",EDGE,"E54");Q56=makeQuery(id+"F0.imprint","IMPRINT",FACE,{"disambiguationData":[TD([[makeQuery(id+"F0.imprint","IMPRINT",EDGE,{"derivedFrom":subQ0}),1.0]])]});}
            var Q57;
            {var subQ0=sQuery(id+"F0.wireOp",EDGE,"E56");Q57=makeQuery(id+"F0.imprint","IMPRINT",FACE,{"disambiguationData":[TD([[makeQuery(id+"F0.imprint","IMPRINT",EDGE,{"derivedFrom":subQ0}),-1.0]])]});}
            var Q58;
            {var subQ0=sQuery(id+"F0.wireOp",EDGE,"E180");Q58=makeQuery(id+"F0.imprint","IMPRINT",FACE,{"disambiguationData":[TD([[makeQuery(id+"F0.imprint","IMPRINT",EDGE,{"derivedFrom":subQ0}),-1.0]])]});}
            var Q59;
            {var subQ6=sQuery(id+"F0.wireOp",EDGE,"E190.MirrorCS");Q59=makeQuery(id+"F0.imprint","IMPRINT",FACE,{"disambiguationData":[TD([[makeQuery(id+"F0.imprint","IMPRINT",EDGE,{"derivedFrom":subQ6}),1.0]])]});}
            var Q60;
            {var subQ6=sQuery(id+"F0.wireOp",EDGE,"E253");Q60=makeQuery(id+"F0.imprint","IMPRINT",FACE,{"disambiguationData":[TD([[makeQuery(id+"F0.imprint","IMPRINT",EDGE,{"derivedFrom":subQ6}),-1.0]])]});}
            var Q61;
            {var subQ2=sQuery(id+"F0.wireOp",EDGE,"E231.MirrorCS");Q61=makeQuery(id+"F0.imprint","IMPRINT",FACE,{"disambiguationData":[TD([[makeQuery(id+"F0.imprint","IMPRINT",EDGE,{"derivedFrom":subQ2}),-1.0]])]});}
            var Q62;
            {var subQ2=sQuery(id+"F0.wireOp",EDGE,"E239");Q62=makeQuery(id+"F0.imprint","IMPRINT",FACE,{"disambiguationData":[TD([[makeQuery(id+"F0.imprint","IMPRINT",EDGE,{"derivedFrom":subQ2}),1.0]])]});}
            var Q63;
            {var subQ0=sQuery(id+"F0.wireOp",EDGE,"E236");Q63=makeQuery(id+"F0.imprint","IMPRINT",FACE,{"disambiguationData":[TD([[makeQuery(id+"F0.imprint","IMPRINT",EDGE,{"derivedFrom":subQ0}),1.0]])]});}
            var Q64;
            {var subQ0=sQuery(id+"F0.wireOp",EDGE,"E240");Q64=makeQuery(id+"F0.imprint","IMPRINT",FACE,{"disambiguationData":[TD([[makeQuery(id+"F0.imprint","IMPRINT",EDGE,{"derivedFrom":subQ0}),1.0]])]});}
            var Q65;
            {var subQ3=sQuery(id+"F0.wireOp",EDGE,"E230");Q65=makeQuery(id+"F0.imprint","IMPRINT",FACE,{"disambiguationData":[TD([[makeQuery(id+"F0.imprint","IMPRINT",EDGE,{"derivedFrom":subQ3}),1.0]])]});}
            extrude(context, id + "F1", {"entities" : qUnion([Q0, Q1, Q2, Q3, Q4, Q5, Q6, Q7, Q8, Q9, Q10, Q11, Q12, Q13, Q14, Q15, Q16, Q17, Q18, Q19, Q20, Q21, Q22, Q23, Q24, Q25, Q26, Q27, Q28, Q29, Q30, Q31, Q32, Q33, Q34, Q35, Q36, Q37, Q38, Q39, Q40, Q41, Q42, Q43, Q44, Q45, Q46, Q47, Q48, Q49, Q50, Q51, Q52, Q53, Q54, Q55, Q56, Q57, Q58, Q59, Q60, Q61, Q62, Q63, Q64, Q65]), "oppositeDirection" : true, "depth" : 3.17 * mm, "offsetDistance" : 25.4 * mm});
        }
        {
            var Q0;
            {var subQ3=sQuery(id+"F0.wireOp",EDGE,"E142.MirrorCS");Q0=makeQuery(id+"F0.imprint","IMPRINT",FACE,{"disambiguationData":[TD([[makeQuery(id+"F0.imprint","IMPRINT",EDGE,{"derivedFrom":subQ3}),1.0]])]});}
            var Q1;
            {var subQ0=sQuery(id+"F0.wireOp",EDGE,"E137.MirrorCS");Q1=makeQuery(id+"F0.imprint","IMPRINT",FACE,{"disambiguationData":[TD([[makeQuery(id+"F0.imprint","IMPRINT",EDGE,{"derivedFrom":subQ0}),-1.0]])]});}
            var Q2;
            {var subQ1=sQuery(id+"F0.wireOp",EDGE,"E23");Q2=makeQuery(id+"F0.imprint","IMPRINT",FACE,{"disambiguationData":[TD([[makeQuery(id+"F0.imprint","IMPRINT",EDGE,{"derivedFrom":subQ1}),1.0]])]});}
            var Q3;
            {var subQ3=sQuery(id+"F0.wireOp",EDGE,"E23");Q3=makeQuery(id+"F0.imprint","IMPRINT",FACE,{"disambiguationData":[TD([[makeQuery(id+"F0.imprint","IMPRINT",EDGE,{"derivedFrom":subQ3}),-1.0]])]});}
            var Q4;
            {var subQ1=sQuery(id+"F0.wireOp",EDGE,"E118.MirrorCS");Q4=makeQuery(id+"F0.imprint","IMPRINT",FACE,{"disambiguationData":[TD([[makeQuery(id+"F0.imprint","IMPRINT",EDGE,{"derivedFrom":subQ1}),1.0]])]});}
            var Q5;
            Q5=makeQuery(id+"F0.imprint","IMPRINT",FACE,{"disambiguationData":[TD([[makeQuery(id+"F0.imprint","IMPRINT",EDGE,{"derivedFrom":sQuery(id+"F0.wireOp",EDGE,"E138.MirrorCS")}),-1.0]])]});
            var Q6;
            Q6=makeQuery(id+"F0.imprint","IMPRINT",FACE,{"disambiguationData":[TD([[makeQuery(id+"F0.imprint","IMPRINT",EDGE,{"derivedFrom":sQuery(id+"F0.wireOp",EDGE,"E80.MirrorCS")}),1.0]])]});
            var Q7;
            Q7=makeQuery(id+"F0.imprint","IMPRINT",FACE,{"disambiguationData":[TD([[makeQuery(id+"F0.imprint","IMPRINT",EDGE,{"derivedFrom":sQuery(id+"F0.wireOp",EDGE,"E1")}),1.0]])]});
            var Q8;
            {var subQ0=sQuery(id+"F0.wireOp",EDGE,"E142.MirrorCS");Q8=makeQuery(id+"F0.imprint","IMPRINT",FACE,{"disambiguationData":[TD([[makeQuery(id+"F0.imprint","IMPRINT",EDGE,{"derivedFrom":subQ0}),-1.0]])]});}
            var Q9;
            {var subQ1=sQuery(id+"F0.wireOp",EDGE,"E142.MirrorCS");Q9=makeQuery(id+"F0.imprint","IMPRINT",FACE,{"disambiguationData":[TD([[makeQuery(id+"F0.imprint","IMPRINT",EDGE,{"derivedFrom":subQ1}),1.0]])]});}
            var Q10;
            {var subQ4=sQuery(id+"F0.wireOp",EDGE,"E118.MirrorCS");Q10=makeQuery(id+"F0.imprint","IMPRINT",FACE,{"disambiguationData":[TD([[makeQuery(id+"F0.imprint","IMPRINT",EDGE,{"derivedFrom":subQ4}),1.0]])]});}
            extrude(context, id + "F2", {"entities" : qUnion([Q0, Q1, Q2, Q3, Q4, Q5, Q6, Q7, Q8, Q9, Q10]), "operationType" : NewBodyOperationType.ADD, "depth" : 3.17 * mm, "offsetDistance" : 25.4 * mm});
        }
        {
            var Q0;
            {var subQ0=sQuery(id+"F0.wireOp",EDGE,"E42");var subQ1=sQuery(id+"F0.wireOp",EDGE,"E27");var subQ2=sQuery(id+"F0.wireOp",EDGE,"E21");Q0=makeQuery(id+"F2.boolean.opBoolean","MERGE",FACE,{"derivedFrom":[makeQuery(id+"F1.opExtrude","SWEPT_FACE",FACE,{"disambiguationData":[OSD([subQ2,subQ0])]}),makeQuery(id+"F1.opExtrude","SWEPT_FACE",FACE,{"disambiguationData":[OSD([subQ1]),TDD([makeQuery(id+"F0.imprint","IMPRINT",EDGE,{"disambiguationData":[TD([[makeQuery(id+"F0.imprint","INTERSECT",VERTEX,{"derivedFrom":[subQ1,sQuery(id+"F0.wireOp",EDGE,"E33")]}),-1.0]])],"derivedFrom":subQ1})])]}),makeQuery(id+"F2.opExtrude","SWEPT_FACE",FACE,{"disambiguationData":[OSD([subQ2,subQ1,subQ0])]})]});}
            var sketch = newSketch(context, id + "F3", { "sketchPlane" : qUnion([Q0])});
            skLineSegment(sketch, "E255.top", {"start": v(-40.78, -3.18) * mm, "end": v(-23, -3.18) * mm});
            skLineSegment(sketch, "E255.left", {"start": v(-40.78, 0) * mm, "end": v(-40.78, -3.18) * mm});
            skLineSegment(sketch, "E255.right", {"start": v(-23, 0) * mm, "end": v(-23, -3.18) * mm});
            skLineSegment(sketch, "E256.top", {"start": v(-95.04, -3.18) * mm, "end": v(-82.34, -3.18) * mm});
            skLineSegment(sketch, "E256.left", {"start": v(-95.04, 0) * mm, "end": v(-95.04, -3.18) * mm});
            skLineSegment(sketch, "E256.right", {"start": v(-82.34, 0) * mm, "end": v(-82.34, -3.18) * mm});
            skLineSegment(sketch, "E257", {"start": v(-23, 0) * mm, "end": v(0, 0) * mm});
            skLineSegment(sketch, "E258", {"start": v(0, 0) * mm, "end": v(0, 11.9) * mm});
            skLineSegment(sketch, "E259", {"start": v(0, 11.9) * mm, "end": v(-23, 11.9) * mm});
            skLineSegment(sketch, "E260", {"start": v(-23, 11.9) * mm, "end": v(-23, 0) * mm});
            skLineSegment(sketch, "E261", {"start": v(0, 5.95) * mm, "end": v(-17.05, 5.95) * mm});
            skCircle(sketch, "E262", {"center": v(-17.05, 5.95) * mm, "radius": 5.95 * mm});
            skLineSegment(sketch, "E263", {"start": v(-17.05, 5.95) * mm, "end": v(-17.05, 11.9) * mm});
            skLineSegment(sketch, "E264", {"start": v(-11.1, 5.95) * mm, "end": v(-8.55, 5.95) * mm});
            skCircle(sketch, "E265", {"center": v(-8.55, 5.95) * mm, "radius": 5.08 * mm});
            skLineSegment(sketch, "E266", {"start": v(-40.78, 0) * mm, "end": v(-82.34, 0) * mm});
            skLineSegment(sketch, "E267", {"start": v(-95.04, 0) * mm, "end": v(-101.4, 0) * mm});
            skLineSegment(sketch, "E268", {"start": v(0, 0) * mm, "end": v(3.81, 0) * mm});
            skLineSegment(sketch, "E269", {"start": v(3.81, 76.2) * mm, "end": v(-6.35, 76.2) * mm});
            skLineSegment(sketch, "E270", {"start": v(-17.05, 5.95) * mm, "end": v(-66.54, 34.53) * mm});
            skCircle(sketch, "E271", {"center": v(-66.54, 34.53) * mm, "radius": 1.65 * mm});
            skLineSegment(sketch, "E272", {"start": v(-15.87, 0.12) * mm, "end": v(-18.22, 0.12) * mm});
            skLineSegment(sketch, "E273", {"start": v(-67.5, 42.67) * mm, "end": v(0.56, 7.98) * mm});
            skLineSegment(sketch, "E274", {"start": v(0.56, 7.98) * mm, "end": v(3.81, 0) * mm});
            skLineSegment(sketch, "E275", {"start": v(-66.54, 34.53) * mm, "end": v(-66.54, 36.18) * mm});
            skLineSegment(sketch, "E276", {"start": v(-66.54, 36.18) * mm, "end": v(-70.02, 36.18) * mm});
            skLineSegment(sketch, "E277", {"start": v(-70.02, 36.18) * mm, "end": v(-54.77, 36.18) * mm});
            skLineSegment(sketch, "E278", {"start": v(-62.1, 36.18) * mm, "end": v(-62.1, 38.72) * mm});
            skLineSegment(sketch, "E279", {"start": v(-62.1, 38.72) * mm, "end": v(-59.75, 38.72) * mm});
            skLineSegment(sketch, "E280", {"start": v(-59.75, 38.72) * mm, "end": v(-67.9, 38.72) * mm});
            skLineSegment(sketch, "E281", {"start": v(-66.54, 36.18) * mm, "end": v(-66.54, 38.72) * mm});
            skLineSegment(sketch, "E282", {"start": v(-66.54, 38.72) * mm, "end": v(-66.54, 41.9) * mm});
            skLineSegment(sketch, "E283", {"start": v(-66.54, 41.9) * mm, "end": v(-61.46, 41.9) * mm});
            skLineSegment(sketch, "E284", {"start": v(-61.46, 41.9) * mm, "end": v(-61.46, 38.72) * mm});
            skLineSegment(sketch, "E285", {"start": v(-67.9, 38.72) * mm, "end": v(-70.02, 36.18) * mm});
            skLineSegment(sketch, "E286", {"start": v(-101.4, 0) * mm, "end": v(-101.4, 5.08) * mm});
            skLineSegment(sketch, "E287", {"start": v(-101.4, 5.08) * mm, "end": v(-79.27, 5.08) * mm});
            skLineSegment(sketch, "E288", {"start": v(-79.27, 5.08) * mm, "end": v(-67.9, 38.72) * mm});
            skLineSegment(sketch, "E289", {"start": v(-66.54, 34.53) * mm, "end": v(-66.54, 0) * mm});
            skLineSegment(sketch, "E290", {"start": v(-66.54, 0) * mm, "end": v(0, 0) * mm});
            skLineSegment(sketch, "E291", {"start": v(-17.05, 5.95) * mm, "end": v(-23, 5.95) * mm});
            skLineSegment(sketch, "E292", {"start": v(-24.6, 10.3) * mm, "end": v(-24.6, 0) * mm});
            skLineSegment(sketch, "E293", {"start": v(-61.81, 31.8) * mm, "end": v(-66.54, 28.22) * mm});
            skSolve(sketch);
        }
        {
            var Q0;
            Q0=makeQuery(id+"F3.imprint","IMPRINT",FACE,{"disambiguationData":[TD([[makeQuery(id+"F3.imprint","IMPRINT",EDGE,{"derivedFrom":sQuery(id+"F3.wireOp",EDGE,"E256.top")}),-1.0]])]});
            var Q1;
            {var subQ0=sQuery(id+"F3.wireOp",EDGE,"E259");var subQ1=sQuery(id+"F3.wireOp",EDGE,"E258");var subQ2=makeQuery(id+"F3.imprint","INTERSECT",VERTEX,{"derivedFrom":[subQ1,subQ0]});Q1=makeQuery(id+"F3.imprint","IMPRINT",FACE,{"disambiguationData":[TD([[makeQuery(id+"F3.imprint","IMPRINT",EDGE,{"disambiguationData":[TD([[subQ2,1.0]])],"derivedFrom":subQ1}),1.0]])]});}
            var Q2;
            {var subQ0=sQuery(id+"F3.wireOp",EDGE,"E283");var subQ1=sQuery(id+"F3.wireOp",EDGE,"E273");var subQ2=makeQuery(id+"F3.imprint","INTERSECT",VERTEX,{"derivedFrom":[subQ1,subQ0]});Q2=makeQuery(id+"F3.imprint","IMPRINT",FACE,{"disambiguationData":[TD([[makeQuery(id+"F3.imprint","IMPRINT",EDGE,{"disambiguationData":[TD([[subQ2,-1.0]])],"derivedFrom":subQ1}),1.0]])]});}
            var Q3;
            {var subQ0=sQuery(id+"F3.wireOp",EDGE,"E285");Q3=makeQuery(id+"F3.imprint","IMPRINT",FACE,{"disambiguationData":[TD([[makeQuery(id+"F3.imprint","IMPRINT",EDGE,{"derivedFrom":subQ0}),1.0]])]});}
            var Q4;
            Q4=makeQuery(id+"F3.imprint","IMPRINT",FACE,{"disambiguationData":[TD([[makeQuery(id+"F3.imprint","IMPRINT",EDGE,{"derivedFrom":sQuery(id+"F3.wireOp",EDGE,"E255.top")}),1.0]])]});
            var Q5;
            {var subQ4=sQuery(id+"F3.wireOp",EDGE,"E268");Q5=makeQuery(id+"F3.imprint","IMPRINT",FACE,{"disambiguationData":[TD([[makeQuery(id+"F3.imprint","IMPRINT",EDGE,{"derivedFrom":subQ4}),1.0]])]});}
            var Q6;
            {var subQ0=sQuery(id+"F3.wireOp",EDGE,"E280");var subQ1=sQuery(id+"F3.wireOp",EDGE,"E273");var subQ2=makeQuery(id+"F3.imprint","INTERSECT",VERTEX,{"derivedFrom":[subQ1,subQ0]});Q6=makeQuery(id+"F3.imprint","IMPRINT",FACE,{"disambiguationData":[TD([[makeQuery(id+"F3.imprint","IMPRINT",EDGE,{"disambiguationData":[TD([[subQ2,1.0]])],"derivedFrom":subQ1}),-1.0]])]});}
            var Q7;
            {var subQ0=sQuery(id+"F3.wireOp",EDGE,"E272");Q7=makeQuery(id+"F3.imprint","IMPRINT",FACE,{"disambiguationData":[TD([[makeQuery(id+"F3.imprint","IMPRINT",EDGE,{"derivedFrom":subQ0}),1.0]])]});}
            var Q8;
            {var subQ0=sQuery(id+"F3.wireOp",EDGE,"E281");Q8=makeQuery(id+"F3.imprint","IMPRINT",FACE,{"disambiguationData":[TD([[makeQuery(id+"F3.imprint","IMPRINT",EDGE,{"derivedFrom":subQ0}),1.0]])]});}
            var Q9;
            {var subQ0=sQuery(id+"F3.wireOp",EDGE,"E262");var subQ1=makeQuery(id+"F3.imprint","INTERSECT",VERTEX,{"disambiguationData":[OD(1.0)],"derivedFrom":[subQ0,sQuery(id+"F3.wireOp",EDGE,"E272")]});Q9=makeQuery(id+"F3.imprint","IMPRINT",FACE,{"disambiguationData":[TD([[makeQuery(id+"F3.imprint","IMPRINT",EDGE,{"disambiguationData":[TD([[subQ1,-1.0]])],"derivedFrom":subQ0}),-1.0]])]});}
            var Q10;
            {var subQ0=sQuery(id+"F3.wireOp",EDGE,"E282");Q10=makeQuery(id+"F3.imprint","IMPRINT",FACE,{"disambiguationData":[TD([[makeQuery(id+"F3.imprint","IMPRINT",EDGE,{"derivedFrom":subQ0}),-1.0]])]});}
            var Q11;
            {var subQ6=sQuery(id+"F3.wireOp",EDGE,"E278");Q11=makeQuery(id+"F3.imprint","IMPRINT",FACE,{"disambiguationData":[TD([[makeQuery(id+"F3.imprint","IMPRINT",EDGE,{"derivedFrom":subQ6}),-1.0]])]});}
            var Q12;
            {var subQ2=sQuery(id+"F3.wireOp",EDGE,"E278");Q12=makeQuery(id+"F3.imprint","IMPRINT",FACE,{"disambiguationData":[TD([[makeQuery(id+"F3.imprint","IMPRINT",EDGE,{"derivedFrom":subQ2}),1.0]])]});}
            var Q13;
            {var subQ4=sQuery(id+"F3.wireOp",EDGE,"E261");var subQ5=sQuery(id+"F3.wireOp",EDGE,"E258");var subQ6=makeQuery(id+"F3.imprint","INTERSECT",VERTEX,{"derivedFrom":[subQ5,subQ4]});Q13=makeQuery(id+"F3.imprint","IMPRINT",FACE,{"disambiguationData":[TD([[makeQuery(id+"F3.imprint","IMPRINT",EDGE,{"disambiguationData":[TD([[subQ6,-1.0]])],"derivedFrom":subQ4}),1.0]])]});}
            var Q14;
            {var subQ7=sQuery(id+"F3.wireOp",EDGE,"E261");var subQ8=sQuery(id+"F3.wireOp",EDGE,"E258");var subQ9=makeQuery(id+"F3.imprint","INTERSECT",VERTEX,{"derivedFrom":[subQ8,subQ7]});Q14=makeQuery(id+"F3.imprint","IMPRINT",FACE,{"disambiguationData":[TD([[makeQuery(id+"F3.imprint","IMPRINT",EDGE,{"disambiguationData":[TD([[subQ9,-1.0]])],"derivedFrom":subQ8}),1.0]])]});}
            var Q15;
            {var subQ0=sQuery(id+"F3.wireOp",EDGE,"E260");var subQ1=sQuery(id+"F3.wireOp",EDGE,"E259");var subQ2=makeQuery(id+"F3.imprint","INTERSECT",VERTEX,{"derivedFrom":[subQ1,subQ0]});Q15=makeQuery(id+"F3.imprint","IMPRINT",FACE,{"disambiguationData":[TD([[makeQuery(id+"F3.imprint","IMPRINT",EDGE,{"disambiguationData":[TD([[subQ2,-1.0]])],"derivedFrom":subQ0}),-1.0]])]});}
            var Q16;
            {var subQ0=sQuery(id+"F0.wireOp",EDGE,"E27");var subQ8=makeQuery(id+"F2.opExtrude","SWEPT_EDGE",EDGE,{"disambiguationData":[OSD([subQ0,sQuery(id+"F0.wireOp",EDGE,"E31")])]});Q16=makeQuery(id+"F3.imprint","IMPRINT",FACE,{"disambiguationData":[TD([[makeQuery(id+"F3.imprint","IMPRINT",EDGE,{"derivedFrom":subQ8}),1.0]])]});}
            var Q17;
            {var subQ0=sQuery(id+"F3.wireOp",EDGE,"E290");var subQ5=sQuery(id+"F3.wireOp",EDGE,"E292");var subQ7=makeQuery(id+"F3.imprint","INTERSECT",VERTEX,{"derivedFrom":[subQ0,subQ5]});Q17=makeQuery(id+"F3.imprint","IMPRINT",FACE,{"disambiguationData":[TD([[makeQuery(id+"F3.imprint","IMPRINT",EDGE,{"disambiguationData":[TD([[subQ7,-1.0]])],"derivedFrom":subQ0}),1.0]])]});}
            var Q18;
            {var subQ9=sQuery(id+"F3.wireOp",EDGE,"E286");Q18=makeQuery(id+"F3.imprint","IMPRINT",FACE,{"disambiguationData":[TD([[makeQuery(id+"F3.imprint","IMPRINT",EDGE,{"derivedFrom":subQ9}),-1.0]])]});}
            var Q19;
            {var subQ1=sQuery(id+"F3.wireOp",EDGE,"E290");var subQ5=makeQuery(id+"F3.imprint","INTERSECT",VERTEX,{"derivedFrom":[sQuery(id+"F3.wireOp",EDGE,"E255.left"),subQ1]});Q19=makeQuery(id+"F3.imprint","IMPRINT",FACE,{"disambiguationData":[TD([[makeQuery(id+"F3.imprint","IMPRINT",EDGE,{"disambiguationData":[TD([[subQ5,-1.0]])],"derivedFrom":subQ1}),1.0]])]});}
            var Q20;
            {var subQ0=sQuery(id+"F3.wireOp",EDGE,"E292");var subQ1=sQuery(id+"F3.wireOp",EDGE,"E270");var subQ2=makeQuery(id+"F3.imprint","INTERSECT",VERTEX,{"derivedFrom":[subQ1,subQ0]});Q20=makeQuery(id+"F3.imprint","IMPRINT",FACE,{"disambiguationData":[TD([[makeQuery(id+"F3.imprint","IMPRINT",EDGE,{"disambiguationData":[TD([[subQ2,1.0]])],"derivedFrom":subQ1}),1.0]])]});}
            var Q21;
            {var subQ0=sQuery(id+"F3.wireOp",EDGE,"E260");var subQ1=sQuery(id+"F3.wireOp",EDGE,"E259");var subQ2=makeQuery(id+"F3.imprint","INTERSECT",VERTEX,{"derivedFrom":[subQ1,subQ0]});Q21=makeQuery(id+"F3.imprint","IMPRINT",FACE,{"disambiguationData":[TD([[makeQuery(id+"F3.imprint","IMPRINT",EDGE,{"disambiguationData":[TD([[subQ2,-1.0]])],"derivedFrom":subQ0}),1.0]])]});}
            var Q22;
            {var subQ0=sQuery(id+"F3.wireOp",EDGE,"E293");Q22=makeQuery(id+"F3.imprint","IMPRINT",FACE,{"disambiguationData":[TD([[makeQuery(id+"F3.imprint","IMPRINT",EDGE,{"derivedFrom":subQ0}),-1.0]])]});}
            extrude(context, id + "F4", {"entities" : qUnion([Q0, Q1, Q2, Q3, Q4, Q5, Q6, Q7, Q8, Q9, Q10, Q11, Q12, Q13, Q14, Q15, Q16, Q17, Q18, Q19, Q20, Q21, Q22]), "depth" : 3.17 * mm, "offsetDistance" : 25.4 * mm});
        }
        {
            var Q0;
            Q0=makeQuery(id+"F4.opExtrude","CAP_FACE",FACE,{"disambiguationData":[OSD([sQuery(id+"F3.wireOp",EDGE,"E255.top"),sQuery(id+"F3.wireOp",EDGE,"E255.left"),sQuery(id+"F3.wireOp",EDGE,"E255.right"),sQuery(id+"F3.wireOp",EDGE,"E257"),sQuery(id+"F3.wireOp",EDGE,"E262"),sQuery(id+"F3.wireOp",EDGE,"E265"),sQuery(id+"F3.wireOp",EDGE,"E266"),sQuery(id+"F3.wireOp",EDGE,"E268"),sQuery(id+"F3.wireOp",EDGE,"E271"),sQuery(id+"F3.wireOp",EDGE,"E272"),sQuery(id+"F3.wireOp",EDGE,"vDhqachQ-1PU0-GfMh-JYSy-m2MrmhNfa3ct"),sQuery(id+"F3.wireOp",EDGE,"E273"),sQuery(id+"F3.wireOp",EDGE,"E274")])],"isStart":false});
            var sketch = newSketch(context, id + "F5", { "sketchPlane" : qUnion([Q0])});
            skCircle(sketch, "E294", {"center": v(-66.54, 34.53) * mm, "radius": 76.2 * mm});
            skLineSegment(sketch, "E295", {"start": v(-66.54, 34.53) * mm, "end": v(-66.54, 36.18) * mm});
            skLineSegment(sketch, "E296", {"start": v(-66.54, 36.18) * mm, "end": v(-70.02, 36.18) * mm});
            skLineSegment(sketch, "E297", {"start": v(-70.02, 36.18) * mm, "end": v(-54.77, 36.18) * mm});
            skLineSegment(sketch, "E298.bottom", {"start": v(-62.4, 36.18) * mm, "end": v(-67.48, 36.18) * mm});
            skLineSegment(sketch, "E298.top", {"start": v(-62.4, 39.35) * mm, "end": v(-67.48, 39.35) * mm});
            skLineSegment(sketch, "E298.left", {"start": v(-62.4, 36.18) * mm, "end": v(-62.4, 39.35) * mm});
            skLineSegment(sketch, "E298.right", {"start": v(-67.48, 36.18) * mm, "end": v(-67.48, 39.35) * mm});
            skLineSegment(sketch, "E299", {"start": v(-62.4, 36.18) * mm, "end": v(-62.4, 0) * mm});
            skLineSegment(sketch, "E300", {"start": v(-62.4, 0) * mm, "end": v(0, 0) * mm});
            skSolve(sketch);
        }
        {
            var Q0;
            Q0=makeQuery(id+"F0.imprint","IMPRINT",FACE,{"disambiguationData":[TD([[makeQuery(id+"F0.imprint","IMPRINT",EDGE,{"derivedFrom":sQuery(id+"F0.wireOp",EDGE,"E161")}),1.0]])]});
            extrude(context, id + "F6", {"entities" : qUnion([Q0]), "depth" : 3.17 * mm, "offsetDistance" : 25.4 * mm});
        }
        {
            var Q0;
            Q0=makeQuery(id+"F6.opExtrude","SWEPT_FACE",FACE,{"disambiguationData":[OSD([sQuery(id+"F0.wireOp",EDGE,"E161")])]});
            var sketch = newSketch(context, id + "F7", { "sketchPlane" : qUnion([Q0])});
            skLineSegment(sketch, "E301.top", {"start": v(-6.04, -3.18) * mm, "end": v(-11.12, -3.18) * mm});
            skLineSegment(sketch, "E301.left", {"start": v(-6.04, 0) * mm, "end": v(-6.04, -3.18) * mm});
            skLineSegment(sketch, "E301.right", {"start": v(-11.12, 0) * mm, "end": v(-11.12, -3.18) * mm});
            skLineSegment(sketch, "E302", {"start": v(-11.12, 0) * mm, "end": v(-36.52, 0) * mm});
            skLineSegment(sketch, "E303.top", {"start": v(-36.52, -3.18) * mm, "end": v(-41.6, -3.18) * mm});
            skLineSegment(sketch, "E303.left", {"start": v(-36.52, 0) * mm, "end": v(-36.52, -3.18) * mm});
            skLineSegment(sketch, "E303.right", {"start": v(-41.6, 0) * mm, "end": v(-41.6, -3.18) * mm});
            skLineSegment(sketch, "E304", {"start": v(-6.04, 0) * mm, "end": v(19.36, 0) * mm});
            skLineSegment(sketch, "E305.top", {"start": v(19.36, -3.17) * mm, "end": v(24.44, -3.17) * mm});
            skLineSegment(sketch, "E305.left", {"start": v(19.36, 0) * mm, "end": v(19.36, -3.17) * mm});
            skLineSegment(sketch, "E305.right", {"start": v(24.44, 0) * mm, "end": v(24.44, -3.17) * mm});
            skLineSegment(sketch, "E306", {"start": v(-41.6, 0) * mm, "end": v(-67, 0) * mm});
            skLineSegment(sketch, "E307.top", {"start": v(-67, -3.18) * mm, "end": v(-72.08, -3.18) * mm});
            skLineSegment(sketch, "E307.left", {"start": v(-67, 0) * mm, "end": v(-67, -3.18) * mm});
            skLineSegment(sketch, "E307.right", {"start": v(-72.08, 0) * mm, "end": v(-72.08, -3.18) * mm});
            skLineSegment(sketch, "E308", {"start": v(24.44, 0) * mm, "end": v(24.44, 5.08) * mm});
            skLineSegment(sketch, "E309", {"start": v(24.44, 5.08) * mm, "end": v(-26.36, 5.08) * mm});
            skLineSegment(sketch, "E310", {"start": v(-26.36, 5.08) * mm, "end": v(-66.42, 41.4) * mm});
            skLineSegment(sketch, "E311", {"start": v(-66.42, 41.4) * mm, "end": v(-82.2, 0) * mm});
            skLineSegment(sketch, "E312", {"start": v(-82.2, 0) * mm, "end": v(-72.08, 0) * mm});
            skLineSegment(sketch, "E313", {"start": v(-61.23, 0) * mm, "end": v(0, 0) * mm});
            skLineSegment(sketch, "E314", {"start": v(0, 0) * mm, "end": v(-65.37, 0) * mm});
            skLineSegment(sketch, "E315", {"start": v(-65.37, 0) * mm, "end": v(-65.37, 34.53) * mm});
            skSolve(sketch);
        }
        {
            var Q0;
            Q0 = qSketchRegion(id + "F7", true);
            extrude(context, id + "F8", {"entities" : qUnion([Q0]), "depth" : 3.17 * mm, "offsetDistance" : 25.4 * mm});
        }
        {
            var Q0;
            Q0=makeQuery(id+"F8.opExtrude","CAP_FACE",FACE,{"disambiguationData":[OSD([sQuery(id+"F7.wireOp",EDGE,"E301.top"),sQuery(id+"F7.wireOp",EDGE,"E301.left"),sQuery(id+"F7.wireOp",EDGE,"E301.right"),sQuery(id+"F7.wireOp",EDGE,"E303.top"),sQuery(id+"F7.wireOp",EDGE,"E303.left"),sQuery(id+"F7.wireOp",EDGE,"E303.right"),sQuery(id+"F7.wireOp",EDGE,"E304"),sQuery(id+"F7.wireOp",EDGE,"E305.top"),sQuery(id+"F7.wireOp",EDGE,"E305.left"),sQuery(id+"F7.wireOp",EDGE,"E305.right"),sQuery(id+"F7.wireOp",EDGE,"E306"),sQuery(id+"F7.wireOp",EDGE,"E307.top"),sQuery(id+"F7.wireOp",EDGE,"E307.left"),sQuery(id+"F7.wireOp",EDGE,"E307.right"),sQuery(id+"F7.wireOp",EDGE,"E308"),sQuery(id+"F7.wireOp",EDGE,"E309"),sQuery(id+"F7.wireOp",EDGE,"E310"),sQuery(id+"F7.wireOp",EDGE,"E311"),sQuery(id+"F7.wireOp",EDGE,"E312"),sQuery(id+"F7.wireOp",EDGE,"E313")])],"isStart":false});
            var sketch = newSketch(context, id + "F9", { "sketchPlane" : qUnion([Q0])});
            skLineSegment(sketch, "E316", {"start": v(-66.42, 41.4) * mm, "end": v(-82.2, 0) * mm});
            skLineSegment(sketch, "E317", {"start": v(-66.42, 41.4) * mm, "end": v(-26.36, 5.08) * mm});
            skLineSegment(sketch, "E318", {"start": v(-26.36, 5.08) * mm, "end": v(24.44, 5.08) * mm});
            skLineSegment(sketch, "E319", {"start": v(24.44, 5.08) * mm, "end": v(24.44, 0) * mm});
            skLineSegment(sketch, "E320", {"start": v(24.44, 0) * mm, "end": v(-82.2, 0) * mm});
            skLineSegment(sketch, "E321", {"start": v(-69.07, 34.44) * mm, "end": v(-64.33, 32.63) * mm});
            skLineSegment(sketch, "E322", {"start": v(-60.91, 36.4) * mm, "end": v(-64.33, 32.63) * mm});
            skLineSegment(sketch, "E323", {"start": v(-64.33, 32.63) * mm, "end": v(-76.76, 0) * mm});
            skLineSegment(sketch, "E324", {"start": v(-64.33, 32.63) * mm, "end": v(-29, 0.61) * mm});
            skLineSegment(sketch, "E325", {"start": v(-29, 0.61) * mm, "end": v(-26.36, 5.08) * mm});
            skLineSegment(sketch, "E326", {"start": v(-29, 0.61) * mm, "end": v(-76.52, 0.61) * mm});
            skLineSegment(sketch, "E327", {"start": v(-64.75, 31.51) * mm, "end": v(-62.6, 30.08) * mm});
            skLineSegment(sketch, "E328", {"start": v(-62.6, 30.08) * mm, "end": v(-62.1, 30.62) * mm});
            skLineSegment(sketch, "E329", {"start": v(-69.15, 19.97) * mm, "end": v(-50.35, 19.97) * mm});
            skLineSegment(sketch, "E330", {"start": v(-69.92, 17.94) * mm, "end": v(-48.11, 17.94) * mm});
            skSolve(sketch);
        }
        {
            var Q0;
            {var subQ1=sQuery(id+"F9.wireOp",EDGE,"E326");Q0=makeQuery(id+"F9.imprint","IMPRINT",FACE,{"disambiguationData":[TD([[makeQuery(id+"F9.imprint","IMPRINT",EDGE,{"derivedFrom":subQ1}),-1.0]])]});}
            var Q1;
            {var subQ1=sQuery(id+"F9.wireOp",EDGE,"E327");Q1=makeQuery(id+"F9.imprint","IMPRINT",FACE,{"disambiguationData":[TD([[makeQuery(id+"F9.imprint","IMPRINT",EDGE,{"derivedFrom":subQ1}),-1.0]])]});}
            extrude(context, id + "F10", {"entities" : qUnion([Q0, Q1]), "operationType" : NewBodyOperationType.REMOVE, "oppositeDirection" : true, "depth" : 3.17 * mm, "offsetDistance" : 25.4 * mm});
        }
        {
            var Q0;
            Q0=makeQuery(id+"F1.opExtrude","CAP_FACE",FACE,{"disambiguationData":[OSD([sQuery(id+"F0.wireOp",EDGE,"E11.MirrorCS"),sQuery(id+"F0.wireOp",EDGE,"E16"),sQuery(id+"F0.wireOp",EDGE,"E21"),sQuery(id+"F0.wireOp",EDGE,"E24"),sQuery(id+"F0.wireOp",EDGE,"E25"),sQuery(id+"F0.wireOp",EDGE,"E26"),sQuery(id+"F0.wireOp",EDGE,"E27"),sQuery(id+"F0.wireOp",EDGE,"E28"),sQuery(id+"F0.wireOp",EDGE,"E31"),sQuery(id+"F0.wireOp",EDGE,"E33"),sQuery(id+"F0.wireOp",EDGE,"E34"),sQuery(id+"F0.wireOp",EDGE,"E35"),sQuery(id+"F0.wireOp",EDGE,"E38"),sQuery(id+"F0.wireOp",EDGE,"E39"),sQuery(id+"F0.wireOp",EDGE,"E42"),sQuery(id+"F0.wireOp",EDGE,"E45.MirrorCS"),sQuery(id+"F0.wireOp",EDGE,"E46.MirrorCS"),sQuery(id+"F0.wireOp",EDGE,"E48"),sQuery(id+"F0.wireOp",EDGE,"E49"),sQuery(id+"F0.wireOp",EDGE,"E50"),sQuery(id+"F0.wireOp",EDGE,"E51"),sQuery(id+"F0.wireOp",EDGE,"E53"),sQuery(id+"F0.wireOp",EDGE,"E55"),sQuery(id+"F0.wireOp",EDGE,"E58"),sQuery(id+"F0.wireOp",EDGE,"E59"),sQuery(id+"F0.wireOp",EDGE,"E60"),sQuery(id+"F0.wireOp",EDGE,"E61"),sQuery(id+"F0.wireOp",EDGE,"E63"),sQuery(id+"F0.wireOp",EDGE,"E64"),sQuery(id+"F0.wireOp",EDGE,"E65"),sQuery(id+"F0.wireOp",EDGE,"E67"),sQuery(id+"F0.wireOp",EDGE,"E68"),sQuery(id+"F0.wireOp",EDGE,"E69"),sQuery(id+"F0.wireOp",EDGE,"E70"),sQuery(id+"F0.wireOp",EDGE,"E71"),sQuery(id+"F0.wireOp",EDGE,"E72"),sQuery(id+"F0.wireOp",EDGE,"E74.left"),sQuery(id+"F0.wireOp",EDGE,"E92.MirrorCS"),sQuery(id+"F0.wireOp",EDGE,"E113.MirrorCS"),sQuery(id+"F0.wireOp",EDGE,"E149.MirrorCS"),sQuery(id+"F0.wireOp",EDGE,"E150.MirrorCS"),sQuery(id+"F0.wireOp",EDGE,"E152"),sQuery(id+"F0.wireOp",EDGE,"E154"),sQuery(id+"F0.wireOp",EDGE,"E155"),sQuery(id+"F0.wireOp",EDGE,"E156"),sQuery(id+"F0.wireOp",EDGE,"E158"),sQuery(id+"F0.wireOp",EDGE,"E159"),sQuery(id+"F0.wireOp",EDGE,"E160"),sQuery(id+"F0.wireOp",EDGE,"E161"),sQuery(id+"F0.wireOp",EDGE,"E162"),sQuery(id+"F0.wireOp",EDGE,"E165"),sQuery(id+"F0.wireOp",EDGE,"E168"),sQuery(id+"F0.wireOp",EDGE,"E171.MirrorCS"),sQuery(id+"F0.wireOp",EDGE,"E172.MirrorCS"),sQuery(id+"F0.wireOp",EDGE,"E173"),sQuery(id+"F0.wireOp",EDGE,"E175"),sQuery(id+"F0.wireOp",EDGE,"E176"),sQuery(id+"F0.wireOp",EDGE,"E177"),sQuery(id+"F0.wireOp",EDGE,"E178"),sQuery(id+"F0.wireOp",EDGE,"E179"),sQuery(id+"F0.wireOp",EDGE,"E180"),sQuery(id+"F0.wireOp",EDGE,"E181"),sQuery(id+"F0.wireOp",EDGE,"E101.MirrorCS"),sQuery(id+"F0.wireOp",EDGE,"E183.MirrorCS"),sQuery(id+"F0.wireOp",EDGE,"E184.MirrorCS"),sQuery(id+"F0.wireOp",EDGE,"E185.MirrorCS"),sQuery(id+"F0.wireOp",EDGE,"E186.MirrorCS"),sQuery(id+"F0.wireOp",EDGE,"E103.MirrorCS"),sQuery(id+"F0.wireOp",EDGE,"E147.MirrorCS"),sQuery(id+"F0.wireOp",EDGE,"E133.MirrorCS"),sQuery(id+"F0.wireOp",EDGE,"E104.MirrorCS"),sQuery(id+"F0.wireOp",EDGE,"E190.MirrorCS"),sQuery(id+"F0.wireOp",EDGE,"E193.MirrorCS"),sQuery(id+"F0.wireOp",EDGE,"E88.MirrorCS"),sQuery(id+"F0.wireOp",EDGE,"E194.MirrorCS"),sQuery(id+"F0.wireOp",EDGE,"E195.MirrorCS"),sQuery(id+"F0.wireOp",EDGE,"E119.MirrorCS"),sQuery(id+"F0.wireOp",EDGE,"E196.MirrorCS"),sQuery(id+"F0.wireOp",EDGE,"E198.MirrorCS"),sQuery(id+"F0.wireOp",EDGE,"E120.MirrorCS"),sQuery(id+"F0.wireOp",EDGE,"E199.MirrorCS"),sQuery(id+"F0.wireOp",EDGE,"E80.MirrorCS"),sQuery(id+"F0.wireOp",EDGE,"E200.MirrorCS"),sQuery(id+"F0.wireOp",EDGE,"E201.MirrorCS"),sQuery(id+"F0.wireOp",EDGE,"E78.MirrorCS"),sQuery(id+"F0.wireOp",EDGE,"E105.MirrorCS"),sQuery(id+"F0.wireOp",EDGE,"E204.MirrorCS"),sQuery(id+"F0.wireOp",EDGE,"E205.MirrorCS"),sQuery(id+"F0.wireOp",EDGE,"E114.MirrorCS"),sQuery(id+"F0.wireOp",EDGE,"E206.MirrorCS"),sQuery(id+"F0.wireOp",EDGE,"E207.MirrorCS"),sQuery(id+"F0.wireOp",EDGE,"E208.MirrorCS"),sQuery(id+"F0.wireOp",EDGE,"E83.MirrorCS"),sQuery(id+"F0.wireOp",EDGE,"E209.MirrorCS"),sQuery(id+"F0.wireOp",EDGE,"E145.MirrorCS"),sQuery(id+"F0.wireOp",EDGE,"E96.MirrorCS"),sQuery(id+"F0.wireOp",EDGE,"E210.MirrorCS"),sQuery(id+"F0.wireOp",EDGE,"E144.MirrorCS"),sQuery(id+"F0.wireOp",EDGE,"E128.MirrorCS"),sQuery(id+"F0.wireOp",EDGE,"E93.MirrorCS"),sQuery(id+"F0.wireOp",EDGE,"E143.MirrorCS"),sQuery(id+"F0.wireOp",EDGE,"E132.MirrorCS"),sQuery(id+"F0.wireOp",EDGE,"E123.MirrorCS"),sQuery(id+"F0.wireOp",EDGE,"E116.MirrorCS"),sQuery(id+"F0.wireOp",EDGE,"E108.MirrorCS"),sQuery(id+"F0.wireOp",EDGE,"E131.MirrorCS"),sQuery(id+"F0.wireOp",EDGE,"E117.MirrorCS"),sQuery(id+"F0.wireOp",EDGE,"E214.MirrorCS"),sQuery(id+"F0.wireOp",EDGE,"E148.top"),sQuery(id+"F0.wireOp",EDGE,"E91.MirrorCS"),sQuery(id+"F0.wireOp",EDGE,"E216.MirrorCS"),sQuery(id+"F0.wireOp",EDGE,"E90.MirrorCS"),sQuery(id+"F0.wireOp",EDGE,"E107.MirrorCS"),sQuery(id+"F0.wireOp",EDGE,"E115.MirrorCS"),sQuery(id+"F0.wireOp",EDGE,"E74.right"),sQuery(id+"F0.wireOp",EDGE,"E129.MirrorCS"),sQuery(id+"F0.wireOp",EDGE,"E106.MirrorCS"),sQuery(id+"F0.wireOp",EDGE,"E94.MirrorCS"),sQuery(id+"F0.wireOp",EDGE,"E148.right"),sQuery(id+"F0.wireOp",EDGE,"E218.MirrorCS"),sQuery(id+"F0.wireOp",EDGE,"E95.MirrorCS"),sQuery(id+"F0.wireOp",EDGE,"E219"),sQuery(id+"F0.wireOp",EDGE,"E220.MirrorCS"),sQuery(id+"F0.wireOp",EDGE,"E223"),sQuery(id+"F0.wireOp",EDGE,"E226"),sQuery(id+"F0.wireOp",EDGE,"E227.MirrorCS"),sQuery(id+"F0.wireOp",EDGE,"E230"),sQuery(id+"F0.wireOp",EDGE,"E231.MirrorCS"),sQuery(id+"F0.wireOp",EDGE,"E232"),sQuery(id+"F0.wireOp",EDGE,"E235.MirrorCS"),sQuery(id+"F0.wireOp",EDGE,"E236"),sQuery(id+"F0.wireOp",EDGE,"E238"),sQuery(id+"F0.wireOp",EDGE,"E239"),sQuery(id+"F0.wireOp",EDGE,"E240"),sQuery(id+"F0.wireOp",EDGE,"E241"),sQuery(id+"F0.wireOp",EDGE,"E243"),sQuery(id+"F0.wireOp",EDGE,"E244"),sQuery(id+"F0.wireOp",EDGE,"E245"),sQuery(id+"F0.wireOp",EDGE,"E246"),sQuery(id+"F0.wireOp",EDGE,"E247.MirrorCS"),sQuery(id+"F0.wireOp",EDGE,"E248.MirrorCS"),sQuery(id+"F0.wireOp",EDGE,"E249.MirrorCS"),sQuery(id+"F0.wireOp",EDGE,"E250.MirrorCS"),sQuery(id+"F0.wireOp",EDGE,"E251.MirrorCS"),sQuery(id+"F0.wireOp",EDGE,"E252.MirrorCS"),sQuery(id+"F0.wireOp",EDGE,"E253"),sQuery(id+"F0.wireOp",EDGE,"E254")])],"isStart":true});
            var sketch = newSketch(context, id + "F11", { "sketchPlane" : qUnion([Q0])});
            skLineSegment(sketch, "E331", {"start": v(-66.74, 0) * mm, "end": v(-66.16, -3.12) * mm});
            skLineSegment(sketch, "E332", {"start": v(-66.16, -3.12) * mm, "end": v(-40.76, -3.12) * mm});
            skLineSegment(sketch, "E333", {"start": v(-40.76, -3.12) * mm, "end": v(-40.76, -19.2) * mm});
            skLineSegment(sketch, "E334", {"start": v(-40.76, -19.2) * mm, "end": v(-65.6, -19.2) * mm});
            skLineSegment(sketch, "E335", {"start": v(-29.08, 4.75) * mm, "end": v(-32.51, 4.75) * mm});
            skLineSegment(sketch, "E336", {"start": v(-30.8, 4.75) * mm, "end": v(-30.8, -2.93) * mm});
            skLineSegment(sketch, "E337.MirrorCS", {"start": v(4.56, -3.12) * mm, "end": v(-20.84, -3.12) * mm});
            skLineSegment(sketch, "E338.MirrorCS", {"start": v(-20.84, -3.12) * mm, "end": v(-20.84, -19.2) * mm});
            skLineSegment(sketch, "E339.MirrorCS", {"start": v(-20.84, -19.2) * mm, "end": v(4, -19.2) * mm});
            skLineSegment(sketch, "E340", {"start": v(-66.16, -3.12) * mm, "end": v(-65.6, -19.2) * mm});
            skLineSegment(sketch, "E341", {"start": v(4.56, -3.12) * mm, "end": v(4, -19.2) * mm});
            skLineSegment(sketch, "E342", {"start": v(-64.77, -23) * mm, "end": v(-65.6, -23) * mm});
            skLineSegment(sketch, "E343", {"start": v(-65.6, -23) * mm, "end": v(-65.6, -19.2) * mm});
            skSolve(sketch);
        }
        {
            var Q0;
            {var subQ5=sQuery(id+"F11.wireOp",EDGE,"E332");Q0=makeQuery(id+"F11.imprint","IMPRINT",FACE,{"disambiguationData":[TD([[makeQuery(id+"F11.imprint","IMPRINT",EDGE,{"derivedFrom":subQ5}),-1.0]])]});}
            var Q1;
            {var subQ4=sQuery(id+"F11.wireOp",EDGE,"E337.MirrorCS");Q1=makeQuery(id+"F11.imprint","IMPRINT",FACE,{"disambiguationData":[TD([[makeQuery(id+"F11.imprint","IMPRINT",EDGE,{"derivedFrom":subQ4}),1.0]])]});}
            extrude(context, id + "F12", {"entities" : qUnion([Q0, Q1]), "operationType" : NewBodyOperationType.REMOVE, "oppositeDirection" : true, "depth" : 25.4 * mm, "offsetDistance" : 25.4 * mm});
        }
        {
            var Q0;
            Q0=sQuery(id+"F5.wireOp",VERTEX,"E295.start");
            var Q1;
            Q1=makeQuery(id+"F8.opExtrude","SWEPT_BODY",BODY,{"disambiguationData":[OSD([sQuery(id+"F7.wireOp",EDGE,"E301.top"),sQuery(id+"F7.wireOp",EDGE,"E301.left"),sQuery(id+"F7.wireOp",EDGE,"E301.right"),sQuery(id+"F7.wireOp",EDGE,"E303.top"),sQuery(id+"F7.wireOp",EDGE,"E303.left"),sQuery(id+"F7.wireOp",EDGE,"E303.right"),sQuery(id+"F7.wireOp",EDGE,"E304"),sQuery(id+"F7.wireOp",EDGE,"E305.top"),sQuery(id+"F7.wireOp",EDGE,"E305.left"),sQuery(id+"F7.wireOp",EDGE,"E305.right"),sQuery(id+"F7.wireOp",EDGE,"E306"),sQuery(id+"F7.wireOp",EDGE,"E307.top"),sQuery(id+"F7.wireOp",EDGE,"E307.left"),sQuery(id+"F7.wireOp",EDGE,"E307.right"),sQuery(id+"F7.wireOp",EDGE,"E308"),sQuery(id+"F7.wireOp",EDGE,"E309"),sQuery(id+"F7.wireOp",EDGE,"E310"),sQuery(id+"F7.wireOp",EDGE,"E311"),sQuery(id+"F7.wireOp",EDGE,"E312"),sQuery(id+"F7.wireOp",EDGE,"E314")])]});
            hole(context, id + "F13", {"style" : HoleStyle.SIMPLE, "endStyle" : HoleEndStyle.BLIND, "oppositeDirection" : true, "holeDiameter" : 3.28 * mm, "majorDiameter" : 6.35 * mm, "holeDepth" : 304.8 * mm, "isTappedThrough" : true, "tappedDepth" : 12.7 * mm, "tapClearance" : 3, "startFromSketch" : true, "locations" : qUnion([Q0]), "scope" : qUnion([Q1])});
        }
    });
